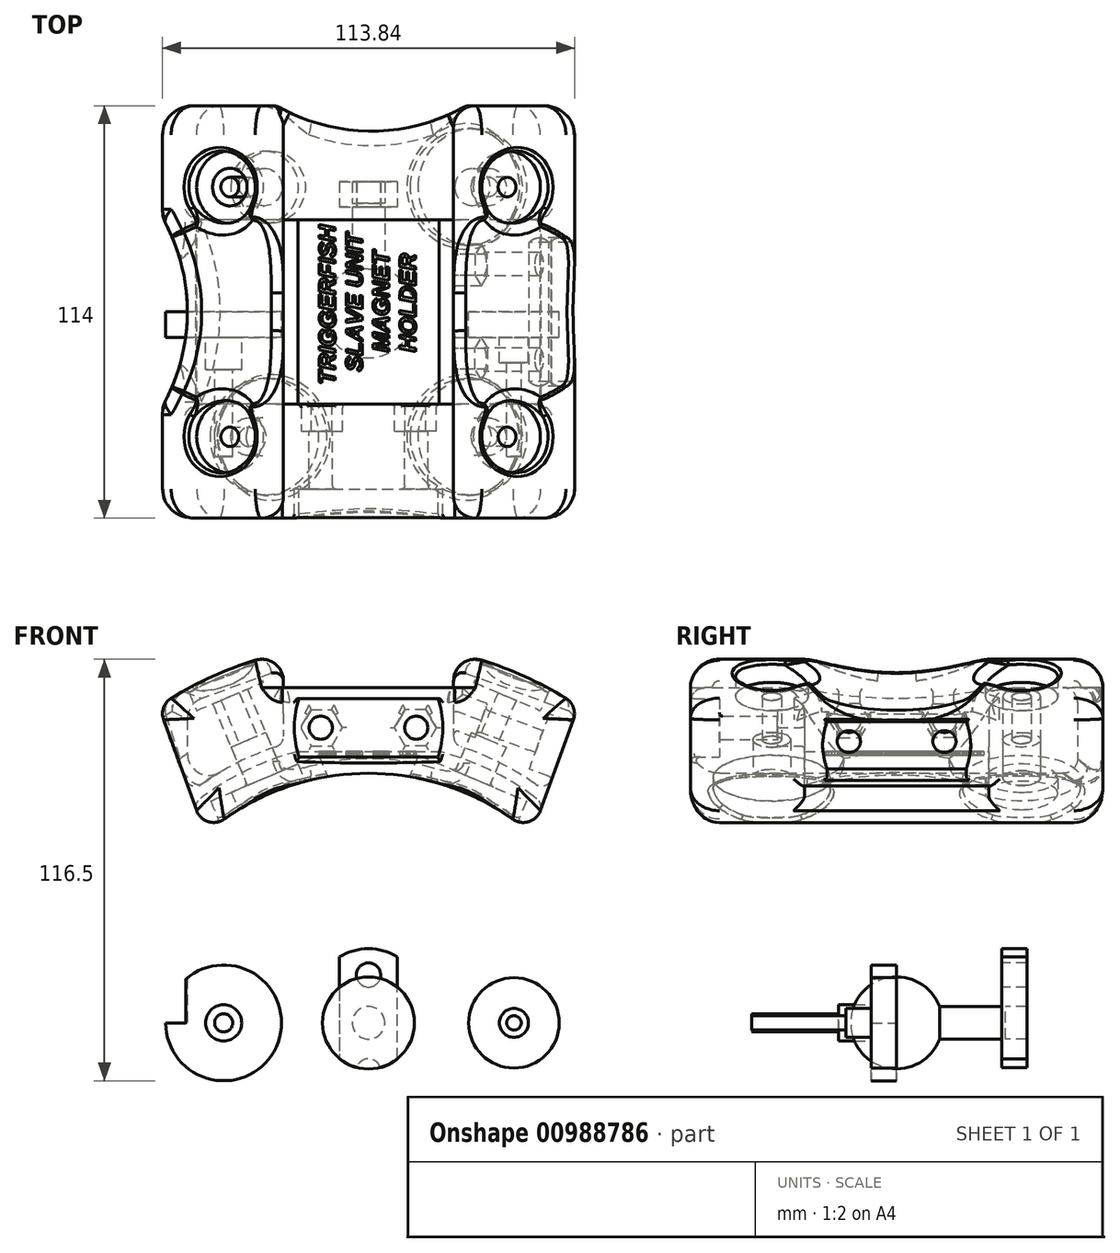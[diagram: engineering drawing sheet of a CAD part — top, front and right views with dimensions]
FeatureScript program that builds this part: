
annotation { "Feature Type Name" : "Feature", "Feature Type Description" : "" }
export const myFeature = defineFeature(function(context is Context, id is Id, definition is map)
    precondition{}
    {
        {
            var Q0;
            Q0=qCreatedBy(makeId("Front.planeOp"),FACE);
            var sketch = newSketch(context, id + "F0", { "sketchPlane" : qUnion([Q0])});
            skLineSegment(sketch, "E0", {"start": v(0, 0) * mm, "end": v(0, 44.71) * mm});
            skLineSegment(sketch, "E1", {"start": v(0, 44.71) * mm, "end": v(-36.6, 82.6) * mm});
            skLineSegment(sketch, "E2", {"start": v(0, 0) * mm, "end": v(-55, 0) * mm, "construction": true});
            skLineSegment(sketch, "E3.MirrorCS", {"start": v(0, 0) * mm, "end": v(55, 0) * mm, "construction": true});
            skArc(sketch, "E4", {"start": v(39.9, 56.3) * mm, "mid": v(0, 69) * mm, "end": v(-39.9, 56.3) * mm});
            skLineSegment(sketch, "E5", {"start": v(55.27, 80.07) * mm, "end": v(47.5, 58.66) * mm});
            skLineSegment(sketch, "E6.trimOffspring", {"start": v(-55, 41.67) * mm, "end": v(-55, 0) * mm, "construction": true});
            skArc(sketch, "E7", {"start": v(56.23, 82.7) * mm, "mid": v(0, 100) * mm, "end": v(-56.23, 82.7) * mm});
            skArc(sketch, "E8", {"start": v(54.51, 89.74) * mm, "mid": v(0, 105) * mm, "end": v(-54.51, 89.74) * mm});
            skLineSegment(sketch, "E9", {"start": v(55.27, 80.07) * mm, "end": v(56.61, 83.76) * mm});
            skLineSegment(sketch, "E10.MirrorCS", {"start": v(-55.27, 80.07) * mm, "end": v(-56.61, 83.76) * mm});
            skPoint(sketch, "E11.visualSharp", {"position": v(57.99, 87.54) * mm});
            skArc(sketch, "E11.filletArc", {"start": v(56.61, 83.76) * mm, "mid": v(56.63, 87.13) * mm, "end": v(54.51, 89.74) * mm});
            skPoint(sketch, "E12.visualSharp", {"position": v(-57.99, 87.54) * mm});
            skArc(sketch, "E12.filletArc", {"start": v(-54.51, 89.74) * mm, "mid": v(-56.63, 87.13) * mm, "end": v(-56.61, 83.76) * mm});
            skLineSegment(sketch, "E13", {"start": v(-55.27, 80.07) * mm, "end": v(-47.5, 58.66) * mm});
            skPoint(sketch, "E14.visualSharp", {"position": v(45.14, 52.19) * mm});
            skArc(sketch, "E14.filletArc", {"start": v(39.9, 56.3) * mm, "mid": v(44.28, 55.6) * mm, "end": v(47.5, 58.66) * mm});
            skPoint(sketch, "E15.visualSharp", {"position": v(-45.14, 52.19) * mm});
            skArc(sketch, "E15.filletArc", {"start": v(-47.5, 58.66) * mm, "mid": v(-44.28, 55.6) * mm, "end": v(-39.9, 56.3) * mm});
            skLineSegment(sketch, "E16.1.0.0", {"start": v(7.78, 66.12) * mm, "end": v(0, 44.71) * mm});
            skSolve(sketch);
        }
        {
            var Q0;
            {var subQ0=sQuery(id+"F0.wireOp",EDGE,"E5");Q0=makeQuery(id+"F0.imprint","IMPRINT",FACE,{"disambiguationData":[TD([[makeQuery(id+"F0.imprint","IMPRINT",EDGE,{"derivedFrom":subQ0}),-1.0]])]});}
            var Q1;
            Q1=makeQuery(id+"F0.imprint","IMPRINT",FACE,{"disambiguationData":[TD([[makeQuery(id+"F0.imprint","IMPRINT",EDGE,{"derivedFrom":sQuery(id+"F0.wireOp",EDGE,"E7")}),-1.0]])]});
            extrude(context, id + "F1", {"entities" : qUnion([Q0, Q1]), "endBound" : BoundingType.SYMMETRIC, "depth" : 114 * mm, "offsetDistance" : 25 * mm, "hasSecondDirection" : true, "secondDirectionOppositeDirection" : true, "secondDirectionDepth" : 53 * mm});
        }
        {
            var Q0;
            Q0=qCreatedBy(makeId("Right.planeOp"),FACE);
            var sketch = newSketch(context, id + "F2", { "sketchPlane" : qUnion([Q0])});
            skLineSegment(sketch, "E17", {"start": v(0, 0) * mm, "end": v(0, 150.3) * mm});
            skLineSegment(sketch, "E18", {"start": v(0, 0) * mm, "end": v(-50, 0) * mm});
            skLineSegment(sketch, "E19", {"start": v(0, 0) * mm, "end": v(50, 0) * mm});
            skLineSegment(sketch, "E20", {"start": v(50, 0) * mm, "end": v(35, 0) * mm});
            skLineSegment(sketch, "E21", {"start": v(-50, 0) * mm, "end": v(-35, 0) * mm});
            skLineSegment(sketch, "E22", {"start": v(-35, 0) * mm, "end": v(-35, 101.57) * mm});
            skLineSegment(sketch, "E23", {"start": v(35, 0) * mm, "end": v(35, 103.74) * mm});
            skLineSegment(sketch, "E24", {"start": v(35, 103.74) * mm, "end": v(-35, 103.74) * mm});
            skLineSegment(sketch, "E25", {"start": v(-35, 103.74) * mm, "end": v(-35, 101.57) * mm});
            skSolve(sketch);
        }
        {
            var Q0;
            Q0=sQuery(id+"F2.wireOp",EDGE,"E18");
            cPlane(context, id + "F3", {"entities" : qUnion([Q0]), "cplaneType" : CPlaneType.LINE_ANGLE, "offset" : 25 * mm, "angle" : 23 * degree, "width" : 150 * mm, "height" : 150 * mm});
        }
        {
            var Q0;
            Q0=qCreatedBy(id+"F3.planeOp",FACE);
            var sketch = newSketch(context, id + "F4", { "sketchPlane" : qUnion([Q0])});
            skLineSegment(sketch, "E26", {"start": v(0, -0.95) * mm, "end": v(0, 31.5) * mm});
            skCircle(sketch, "E27", {"center": v(0, 34.5) * mm, "radius": 2.7 * mm});
            skCircle(sketch, "E28", {"center": v(0, 34.5) * mm, "radius": 16.2 * mm});
            skCircle(sketch, "E29.MirrorC", {"center": v(0, -34.5) * mm, "radius": 2.7 * mm});
            skCircle(sketch, "E30.MirrorC", {"center": v(0, -34.5) * mm, "radius": 16.2 * mm});
            skCircle(sketch, "E31", {"center": v(0, 34.5) * mm, "radius": 5.2 * mm});
            skCircle(sketch, "E32", {"center": v(0, 34.5) * mm, "radius": 10 * mm});
            skCircle(sketch, "E33", {"center": v(0, -34.5) * mm, "radius": 10 * mm});
            skCircle(sketch, "E34", {"center": v(0, -34.5) * mm, "radius": 5.2 * mm});
            skSolve(sketch);
        }
        {
            var Q0;
            Q0=makeQuery(id+"F4.imprint","IMPRINT",FACE,{"disambiguationData":[TD([[makeQuery(id+"F4.imprint","IMPRINT",EDGE,{"derivedFrom":sQuery(id+"F4.wireOp",EDGE,"E27")}),1.0]])]});
            var Q1;
            Q1=makeQuery(id+"F4.imprint","IMPRINT",FACE,{"disambiguationData":[TD([[makeQuery(id+"F4.imprint","IMPRINT",EDGE,{"derivedFrom":sQuery(id+"F4.wireOp",EDGE,"E29.MirrorC")}),-1.0]])]});
            extrude(context, id + "F5", {"entities" : qUnion([Q0, Q1]), "operationType" : NewBodyOperationType.REMOVE, "endBound" : BoundingType.THROUGH_ALL, "oppositeDirection" : true, "depth" : 131 * mm, "offsetDistance" : 25 * mm});
        }
        {
            var Q0;
            Q0=makeQuery(id+"F4.imprint","IMPRINT",FACE,{"disambiguationData":[TD([[makeQuery(id+"F4.imprint","IMPRINT",EDGE,{"derivedFrom":sQuery(id+"F4.wireOp",EDGE,"7e92ca80-ed04-4259-94b1-b0eb367302a11.MirrorC")}),1.0]])]});
            var Q1;
            Q1=makeQuery(id+"F4.imprint","IMPRINT",FACE,{"disambiguationData":[TD([[makeQuery(id+"F4.imprint","IMPRINT",EDGE,{"derivedFrom":sQuery(id+"F4.wireOp",EDGE,"7e92ca80-ed04-4259-94b1-b0eb367302a11.MirrorC")}),-1.0]])]});
            var Q2;
            Q2=makeQuery(id+"F4.imprint","IMPRINT",FACE,{"disambiguationData":[TD([[makeQuery(id+"F4.imprint","IMPRINT",EDGE,{"derivedFrom":sQuery(id+"F4.wireOp",EDGE,"drXH0XQP-8KRI-Yurm-uRQJ-bzc3cydU0AWB")}),1.0]])]});
            var Q3;
            Q3=makeQuery(id+"F4.imprint","IMPRINT",FACE,{"disambiguationData":[TD([[makeQuery(id+"F4.imprint","IMPRINT",EDGE,{"derivedFrom":sQuery(id+"F4.wireOp",EDGE,"E27")}),-1.0]])]});
            var Q4;
            Q4=makeQuery(id+"F4.imprint","IMPRINT",FACE,{"disambiguationData":[TD([[makeQuery(id+"F4.imprint","IMPRINT",EDGE,{"derivedFrom":sQuery(id+"F4.wireOp",EDGE,"E30.MirrorC")}),-1.0]])]});
            var Q5;
            Q5=makeQuery(id+"F4.imprint","IMPRINT",FACE,{"disambiguationData":[TD([[makeQuery(id+"F4.imprint","IMPRINT",EDGE,{"derivedFrom":sQuery(id+"F4.wireOp",EDGE,"E28")}),1.0]])]});
            var Q6;
            Q6=makeQuery(id+"F4.imprint","IMPRINT",FACE,{"disambiguationData":[TD([[makeQuery(id+"F4.imprint","IMPRINT",EDGE,{"derivedFrom":sQuery(id+"F4.wireOp",EDGE,"E31")}),-1.0]])]});
            var Q7;
            Q7=makeQuery(id+"F4.imprint","IMPRINT",FACE,{"disambiguationData":[TD([[makeQuery(id+"F4.imprint","IMPRINT",EDGE,{"derivedFrom":sQuery(id+"F4.wireOp",EDGE,"iOXqjNKU-hcXU-oM97-z01q-G4LAReMeK2zs")}),-1.0]])]});
            var Q8;
            Q8=makeQuery(id+"F4.imprint","IMPRINT",FACE,{"disambiguationData":[TD([[makeQuery(id+"F4.imprint","IMPRINT",EDGE,{"derivedFrom":sQuery(id+"F4.wireOp",EDGE,"E33")}),1.0]])]});
            var Q9;
            Q9=makeQuery(id+"F4.imprint","IMPRINT",FACE,{"disambiguationData":[TD([[makeQuery(id+"F4.imprint","IMPRINT",EDGE,{"derivedFrom":sQuery(id+"F4.wireOp",EDGE,"E29.MirrorC")}),1.0]])]});
            extrude(context, id + "F6", {"entities" : qUnion([Q0, Q1, Q2, Q3, Q4, Q5, Q6, Q7, Q8, Q9]), "operationType" : NewBodyOperationType.REMOVE, "oppositeDirection" : true, "depth" : 73.5 * mm, "offsetDistance" : 25 * mm});
        }
        {
            var Q0;
            Q0=makeQuery(id+"F4.imprint","IMPRINT",FACE,{"disambiguationData":[TD([[makeQuery(id+"F4.imprint","IMPRINT",EDGE,{"derivedFrom":sQuery(id+"F4.wireOp",EDGE,"E27")}),-1.0]])]});
            var Q1;
            Q1=makeQuery(id+"F4.imprint","IMPRINT",FACE,{"disambiguationData":[TD([[makeQuery(id+"F4.imprint","IMPRINT",EDGE,{"derivedFrom":sQuery(id+"F4.wireOp",EDGE,"E29.MirrorC")}),1.0]])]});
            extrude(context, id + "F7", {"entities" : qUnion([Q0, Q1]), "operationType" : NewBodyOperationType.REMOVE, "oppositeDirection" : true, "depth" : 85 * mm, "hasOffset" : true, "offsetDistance" : 18 * mm});
        }
        {
            var Q0;
            Q0=makeQuery(id+"F4.imprint","IMPRINT",FACE,{"disambiguationData":[TD([[makeQuery(id+"F4.imprint","IMPRINT",EDGE,{"derivedFrom":sQuery(id+"F4.wireOp",EDGE,"7e92ca80-ed04-4259-94b1-b0eb367302a11.MirrorC")}),-1.0]])]});
            var Q1;
            Q1=makeQuery(id+"F4.imprint","IMPRINT",FACE,{"disambiguationData":[TD([[makeQuery(id+"F4.imprint","IMPRINT",EDGE,{"derivedFrom":sQuery(id+"F4.wireOp",EDGE,"E29.MirrorC")}),1.0]])]});
            var Q2;
            Q2=makeQuery(id+"F4.imprint","IMPRINT",FACE,{"disambiguationData":[TD([[makeQuery(id+"F4.imprint","IMPRINT",EDGE,{"derivedFrom":sQuery(id+"F4.wireOp",EDGE,"drXH0XQP-8KRI-Yurm-uRQJ-bzc3cydU0AWB")}),1.0]])]});
            var Q3;
            Q3=makeQuery(id+"F4.imprint","IMPRINT",FACE,{"disambiguationData":[TD([[makeQuery(id+"F4.imprint","IMPRINT",EDGE,{"derivedFrom":sQuery(id+"F4.wireOp",EDGE,"E27")}),-1.0]])]});
            var Q4;
            Q4=makeQuery(id+"F4.imprint","IMPRINT",FACE,{"disambiguationData":[TD([[makeQuery(id+"F4.imprint","IMPRINT",EDGE,{"derivedFrom":sQuery(id+"F4.wireOp",EDGE,"iOXqjNKU-hcXU-oM97-z01q-G4LAReMeK2zs")}),-1.0]])]});
            var Q5;
            Q5=makeQuery(id+"F4.imprint","IMPRINT",FACE,{"disambiguationData":[TD([[makeQuery(id+"F4.imprint","IMPRINT",EDGE,{"derivedFrom":sQuery(id+"F4.wireOp",EDGE,"E31")}),-1.0]])]});
            var Q6;
            Q6=makeQuery(id+"F4.imprint","IMPRINT",FACE,{"disambiguationData":[TD([[makeQuery(id+"F4.imprint","IMPRINT",EDGE,{"derivedFrom":sQuery(id+"F4.wireOp",EDGE,"E33")}),1.0]])]});
            extrude(context, id + "F8", {"entities" : qUnion([Q0, Q1, Q2, Q3, Q4, Q5, Q6]), "operationType" : NewBodyOperationType.REMOVE, "endBound" : BoundingType.THROUGH_ALL, "oppositeDirection" : true, "depth" : 25 * mm, "offsetDistance" : 25 * mm, "hasSecondDirection" : true, "secondDirectionOppositeDirection" : true, "secondDirectionDepth" : 98 * mm});
        }
        {
            var Q0;
            Q0=sQuery(id+"F4.wireOp",EDGE,"E26");
            cPlane(context, id + "F9", {"entities" : qUnion([Q0]), "cplaneType" : CPlaneType.LINE_ANGLE, "offset" : 25 * mm, "angle" : 23 * degree, "oppositeDirection" : true, "width" : 150 * mm, "height" : 150 * mm});
        }
        {
            var Q0;
            Q0=sQuery(id+"F2.wireOp",EDGE,"E18");
            cPlane(context, id + "F10", {"entities" : qUnion([Q0]), "cplaneType" : CPlaneType.LINE_ANGLE, "offset" : 25 * mm, "angle" : 104 * degree, "oppositeDirection" : true, "width" : 150 * mm, "height" : 150 * mm});
        }
        {
            var Q0;
            Q0=qCreatedBy(id+"F9.planeOp",FACE);
            var sketch = newSketch(context, id + "F11", { "sketchPlane" : qUnion([Q0])});
            skCircle(sketch, "E35", {"center": v(0, -34.5) * mm, "radius": 16.2 * mm});
            skCircle(sketch, "E36", {"center": v(0, -34.5) * mm, "radius": 10 * mm});
            skCircle(sketch, "E37", {"center": v(0, -34.5) * mm, "radius": 2.7 * mm});
            skCircle(sketch, "E38", {"center": v(0, 34.5) * mm, "radius": 2.7 * mm});
            skCircle(sketch, "E39", {"center": v(0, 34.5) * mm, "radius": 10 * mm});
            skCircle(sketch, "E40", {"center": v(0, 34.5) * mm, "radius": 16.2 * mm});
            skCircle(sketch, "E41", {"center": v(0, -34.5) * mm, "radius": 5.2 * mm});
            skCircle(sketch, "E42", {"center": v(0, 34.5) * mm, "radius": 5.2 * mm});
            skSolve(sketch);
        }
        {
            var Q0;
            Q0=makeQuery(id+"F11.imprint","IMPRINT",FACE,{"disambiguationData":[TD([[makeQuery(id+"F11.imprint","IMPRINT",EDGE,{"derivedFrom":sQuery(id+"F11.wireOp",EDGE,"E38")}),1.0]])]});
            var Q1;
            Q1=makeQuery(id+"F11.imprint","IMPRINT",FACE,{"disambiguationData":[TD([[makeQuery(id+"F11.imprint","IMPRINT",EDGE,{"derivedFrom":sQuery(id+"F11.wireOp",EDGE,"E37")}),1.0]])]});
            var Q2;
            Q2=sQuery(id+"F11.wireOp",EDGE,"E38");
            extrude(context, id + "F12", {"entities" : qUnion([Q0, Q1]), "operationType" : NewBodyOperationType.REMOVE, "surfaceEntities" : qUnion([Q2]), "endBound" : BoundingType.THROUGH_ALL, "oppositeDirection" : true, "depth" : 25 * mm, "offsetDistance" : 25 * mm});
        }
        {
            var Q0;
            Q0=makeQuery(id+"F11.imprint","IMPRINT",FACE,{"disambiguationData":[TD([[makeQuery(id+"F11.imprint","IMPRINT",EDGE,{"derivedFrom":sQuery(id+"F11.wireOp",EDGE,"E35")}),-1.0]])]});
            var Q1;
            Q1=makeQuery(id+"F11.imprint","IMPRINT",FACE,{"disambiguationData":[TD([[makeQuery(id+"F11.imprint","IMPRINT",EDGE,{"derivedFrom":sQuery(id+"F11.wireOp",EDGE,"E35")}),1.0]])]});
            var Q2;
            Q2=makeQuery(id+"F11.imprint","IMPRINT",FACE,{"disambiguationData":[TD([[makeQuery(id+"F11.imprint","IMPRINT",EDGE,{"derivedFrom":sQuery(id+"F11.wireOp",EDGE,"E39")}),-1.0]])]});
            var Q3;
            Q3=makeQuery(id+"F11.imprint","IMPRINT",FACE,{"disambiguationData":[TD([[makeQuery(id+"F11.imprint","IMPRINT",EDGE,{"derivedFrom":sQuery(id+"F11.wireOp",EDGE,"E39")}),1.0]])]});
            var Q4;
            Q4=makeQuery(id+"F11.imprint","IMPRINT",FACE,{"disambiguationData":[TD([[makeQuery(id+"F11.imprint","IMPRINT",EDGE,{"derivedFrom":sQuery(id+"F11.wireOp",EDGE,"E37")}),-1.0]])]});
            var Q5;
            Q5=makeQuery(id+"F11.imprint","IMPRINT",FACE,{"disambiguationData":[TD([[makeQuery(id+"F11.imprint","IMPRINT",EDGE,{"derivedFrom":sQuery(id+"F11.wireOp",EDGE,"E38")}),-1.0]])]});
            var Q6;
            Q6=makeQuery(id+"F11.imprint","IMPRINT",FACE,{"disambiguationData":[TD([[makeQuery(id+"F11.imprint","IMPRINT",EDGE,{"derivedFrom":sQuery(id+"F11.wireOp",EDGE,"E36")}),1.0]])]});
            var Q7;
            Q7=makeQuery(id+"F1.opExtrude","SWEPT_FACE",FACE,{"disambiguationData":[OSD([sQuery(id+"F0.wireOp",EDGE,"qRGGQMld-MaHZ-AlMi-78vc-qT90qwAjfGs4")])]});
            extrude(context, id + "F13", {"entities" : qUnion([Q0, Q1, Q2, Q3, Q4, Q5, Q6]), "operationType" : NewBodyOperationType.REMOVE, "oppositeDirection" : true, "depth" : 73.5 * mm, "endBoundEntityFace" : qUnion([Q7]), "offsetDistance" : 25 * mm});
        }
        {
            var Q0;
            Q0=sQuery(id+"F0.wireOp",EDGE,"E16.1.0.0");
            cPlane(context, id + "F14", {"entities" : qUnion([Q0]), "cplaneType" : CPlaneType.LINE_ANGLE, "offset" : 25 * mm, "angle" : 180 * degree, "width" : 150 * mm, "height" : 150 * mm});
        }
        {
            var Q0;
            Q0=makeQuery(id+"F11.imprint","IMPRINT",FACE,{"disambiguationData":[TD([[makeQuery(id+"F11.imprint","IMPRINT",EDGE,{"derivedFrom":sQuery(id+"F11.wireOp",EDGE,"E36")}),1.0]])]});
            var Q1;
            Q1=makeQuery(id+"F11.imprint","IMPRINT",FACE,{"disambiguationData":[TD([[makeQuery(id+"F11.imprint","IMPRINT",EDGE,{"derivedFrom":sQuery(id+"F11.wireOp",EDGE,"E37")}),-1.0]])]});
            var Q2;
            Q2=makeQuery(id+"F11.imprint","IMPRINT",FACE,{"disambiguationData":[TD([[makeQuery(id+"F11.imprint","IMPRINT",EDGE,{"derivedFrom":sQuery(id+"F11.wireOp",EDGE,"E39")}),1.0]])]});
            var Q3;
            Q3=makeQuery(id+"F11.imprint","IMPRINT",FACE,{"disambiguationData":[TD([[makeQuery(id+"F11.imprint","IMPRINT",EDGE,{"derivedFrom":sQuery(id+"F11.wireOp",EDGE,"E38")}),-1.0]])]});
            extrude(context, id + "F15", {"entities" : qUnion([Q0, Q1, Q2, Q3]), "operationType" : NewBodyOperationType.REMOVE, "endBound" : BoundingType.THROUGH_ALL, "oppositeDirection" : true, "depth" : 25 * mm, "offsetDistance" : 25 * mm, "hasSecondDirection" : true, "secondDirectionOppositeDirection" : true, "secondDirectionDepth" : 98 * mm});
        }
        {
            var Q0;
            Q0=makeQuery(id+"F11.imprint","IMPRINT",FACE,{"disambiguationData":[TD([[makeQuery(id+"F11.imprint","IMPRINT",EDGE,{"derivedFrom":sQuery(id+"F11.wireOp",EDGE,"E37")}),-1.0]])]});
            var Q1;
            Q1=makeQuery(id+"F11.imprint","IMPRINT",FACE,{"disambiguationData":[TD([[makeQuery(id+"F11.imprint","IMPRINT",EDGE,{"derivedFrom":sQuery(id+"F11.wireOp",EDGE,"E38")}),-1.0]])]});
            extrude(context, id + "F16", {"entities" : qUnion([Q0, Q1]), "operationType" : NewBodyOperationType.REMOVE, "oppositeDirection" : true, "depth" : 85 * mm, "offsetDistance" : 25 * mm});
        }
        {
            var Q0;
            Q0=qCreatedBy(makeId("Top.planeOp"),FACE);
            var sketch = newSketch(context, id + "F17", { "sketchPlane" : qUnion([Q0])});
            skLineSegment(sketch, "E43", {"start": v(40, 0) * mm, "end": v(40, -72) * mm});
            skLineSegment(sketch, "E44", {"start": v(40, -72) * mm, "end": v(-40, -72) * mm});
            skLineSegment(sketch, "E45", {"start": v(-40, -72) * mm, "end": v(-40, 72) * mm});
            skLineSegment(sketch, "E46", {"start": v(-40, 72) * mm, "end": v(40, 72) * mm});
            skLineSegment(sketch, "E47", {"start": v(40, 72) * mm, "end": v(40, 0) * mm});
            skLineSegment(sketch, "E48", {"start": v(0, 0) * mm, "end": v(-84.9, 0) * mm, "construction": true});
            skLineSegment(sketch, "E49", {"start": v(-40, -72) * mm, "end": v(-40, -52) * mm});
            skLineSegment(sketch, "E50", {"start": v(-40, -52) * mm, "end": v(-20, -52) * mm, "construction": true});
            skLineSegment(sketch, "E51", {"start": v(-20, -52) * mm, "end": v(20, -52) * mm, "construction": true});
            skLineSegment(sketch, "E52", {"start": v(20, -52) * mm, "end": v(40, -52) * mm, "construction": true});
            skLineSegment(sketch, "E53", {"start": v(0, 0) * mm, "end": v(55.62, 0) * mm, "construction": true});
            skArc(sketch, "E54", {"start": v(-40, -52) * mm, "mid": v(-34.14, -66.14) * mm, "end": v(-20, -72) * mm});
            skLineSegment(sketch, "E55", {"start": v(-40, 0) * mm, "end": v(-30, 0) * mm});
            skLineSegment(sketch, "E56", {"start": v(-40, 72) * mm, "end": v(-40, 52) * mm});
            skArc(sketch, "E57", {"start": v(-20, 72) * mm, "mid": v(-34.14, 66.14) * mm, "end": v(-40, 52) * mm});
            skFitSpline(sketch, "E58", {"points": [v(-40, -52) * mm, v(-30, 0) * mm, v(-40, 52) * mm], "startDerivative": vector(30, 104) * mm, "endDerivative": vector(-30, 104) * mm});
            skLineSegment(sketch, "E59", {"start": v(0, -30.04) * mm, "end": v(0, 13.28) * mm, "construction": true});
            skFitSpline(sketch, "E60.MirrorCS", {"points": [v(40, -52) * mm, v(30, 0) * mm, v(40, 52) * mm], "startDerivative": vector(-30, 104) * mm, "endDerivative": vector(30, 104) * mm});
            skArc(sketch, "E61.MirrorCS", {"start": v(40, -52) * mm, "mid": v(34.14, -66.14) * mm, "end": v(20, -72) * mm});
            skArc(sketch, "E62.MirrorCS", {"start": v(20, 72) * mm, "mid": v(34.14, 66.14) * mm, "end": v(40, 52) * mm});
            skLineSegment(sketch, "E63", {"start": v(0, -30.04) * mm, "end": v(0, -72) * mm, "construction": true});
            skLineSegment(sketch, "E64", {"start": v(0, -72) * mm, "end": v(0, -68.5) * mm, "construction": true});
            skArc(sketch, "E65", {"start": v(20, -72) * mm, "mid": v(0, -69.08) * mm, "end": v(-20, -72) * mm});
            skArc(sketch, "E66.MirrorCS", {"start": v(20, 72) * mm, "mid": v(0, 69.08) * mm, "end": v(-20, 72) * mm});
            skSolve(sketch);
        }
        {
            var Q0;
            Q0=qCreatedBy(id+"F14.planeOp",FACE);
            var sketch = newSketch(context, id + "F18", { "sketchPlane" : qUnion([Q0])});
            skLineSegment(sketch, "E67", {"start": v(-19.2, 81.07) * mm, "end": v(0, 81.07) * mm});
            skLineSegment(sketch, "E68", {"start": v(-19.2, 97.27) * mm, "end": v(19.2, 97.27) * mm});
            skLineSegment(sketch, "E69", {"start": v(19.2, 81.07) * mm, "end": v(0, 81.07) * mm});
            skPoint(sketch, "E70.endSnap0", {"position": v(-18.2, 89.17) * mm});
            skLineSegment(sketch, "E71.0", {"start": v(10.1, 94.17) * mm, "end": v(15.87, 94.17) * mm});
            skLineSegment(sketch, "E71.1", {"start": v(15.87, 94.17) * mm, "end": v(18.75, 89.17) * mm});
            skLineSegment(sketch, "E71.2", {"start": v(18.75, 89.17) * mm, "end": v(15.87, 84.17) * mm});
            skLineSegment(sketch, "E71.3", {"start": v(15.87, 84.17) * mm, "end": v(10.1, 84.17) * mm});
            skLineSegment(sketch, "E71.4", {"start": v(10.1, 84.17) * mm, "end": v(7.2, 89.17) * mm});
            skLineSegment(sketch, "E71.5", {"start": v(7.2, 89.17) * mm, "end": v(10.1, 94.17) * mm});
            skPoint(sketch, "E71.0.midPoint", {"position": v(11.28, 94.17) * mm});
            skLineSegment(sketch, "E72.MirrorCS", {"start": v(-15.87, 84.17) * mm, "end": v(-10.1, 84.17) * mm});
            skLineSegment(sketch, "E73.MirrorCS", {"start": v(-18.75, 89.17) * mm, "end": v(-15.87, 84.17) * mm});
            skLineSegment(sketch, "E74.MirrorCS", {"start": v(-15.87, 94.17) * mm, "end": v(-18.75, 89.17) * mm});
            skLineSegment(sketch, "E75.MirrorCS", {"start": v(-10.1, 94.17) * mm, "end": v(-15.87, 94.17) * mm});
            skLineSegment(sketch, "E76.MirrorCS", {"start": v(-10.1, 84.17) * mm, "end": v(-7.2, 89.17) * mm});
            skLineSegment(sketch, "E77.MirrorCS", {"start": v(-7.2, 89.17) * mm, "end": v(-10.1, 94.17) * mm});
            skLineSegment(sketch, "E78", {"start": v(0, 81.17) * mm, "end": v(0, 101.62) * mm, "construction": true});
            skArc(sketch, "E79", {"start": v(-19.2, 97.27) * mm, "mid": v(-20.5, 89.17) * mm, "end": v(-19.2, 81.07) * mm});
            skArc(sketch, "E80.MirrorCS", {"start": v(19.2, 97.27) * mm, "mid": v(20.5, 89.17) * mm, "end": v(19.2, 81.07) * mm});
            skCircle(sketch, "E81", {"center": v(-13.2, 89.17) * mm, "radius": 3.2 * mm});
            skCircle(sketch, "E82", {"center": v(13.2, 89.17) * mm, "radius": 3.2 * mm});
            skSolve(sketch);
        }
        {
            var Q0;
            {var subQ4=sQuery(id+"F18.wireOp",EDGE,"E69");Q0=makeQuery(id+"F18.imprint","IMPRINT",FACE,{"disambiguationData":[TD([[makeQuery(id+"F18.imprint","IMPRINT",EDGE,{"derivedFrom":subQ4}),-1.0]])]});}
            var Q1;
            {var subQ0=sQuery(id+"F18.wireOp",EDGE,"E67");Q1=makeQuery(id+"F18.imprint","IMPRINT",FACE,{"disambiguationData":[TD([[makeQuery(id+"F18.imprint","IMPRINT",EDGE,{"derivedFrom":subQ0}),1.0]])]});}
            var Q2;
            Q2=makeQuery(id+"F18.imprint","IMPRINT",FACE,{"disambiguationData":[TD([[makeQuery(id+"F18.imprint","IMPRINT",EDGE,{"derivedFrom":sQuery(id+"F18.wireOp",EDGE,"f1425f39-42cd-430a-935a-0037c350caf40.MirrorC")}),1.0]])]});
            var Q3;
            Q3=makeQuery(id+"F18.imprint","IMPRINT",FACE,{"disambiguationData":[TD([[makeQuery(id+"F18.imprint","IMPRINT",EDGE,{"derivedFrom":sQuery(id+"F18.wireOp",EDGE,"f1425f39-42cd-430a-935a-0037c350caf40.MirrorC")}),-1.0]])]});
            var Q4;
            Q4=makeQuery(id+"F18.imprint","IMPRINT",FACE,{"disambiguationData":[TD([[makeQuery(id+"F18.imprint","IMPRINT",EDGE,{"derivedFrom":sQuery(id+"F18.wireOp",EDGE,"a20799b0-e35e-4c22-ab32-daaa3fd97331")}),1.0]])]});
            var Q5;
            Q5=makeQuery(id+"F18.imprint","IMPRINT",FACE,{"disambiguationData":[TD([[makeQuery(id+"F18.imprint","IMPRINT",EDGE,{"derivedFrom":sQuery(id+"F18.wireOp",EDGE,"a20799b0-e35e-4c22-ab32-daaa3fd97331")}),-1.0]])]});
            var Q6;
            Q6=makeQuery(id+"F18.imprint","IMPRINT",FACE,{"disambiguationData":[TD([[makeQuery(id+"F18.imprint","IMPRINT",EDGE,{"derivedFrom":sQuery(id+"F18.wireOp",EDGE,"E71.0")}),-1.0]])]});
            var Q7;
            Q7=makeQuery(id+"F18.imprint","IMPRINT",FACE,{"disambiguationData":[TD([[makeQuery(id+"F18.imprint","IMPRINT",EDGE,{"derivedFrom":sQuery(id+"F18.wireOp",EDGE,"E72.MirrorCS")}),1.0]])]});
            extrude(context, id + "F19", {"entities" : qUnion([Q0, Q1, Q2, Q3, Q4, Q5, Q6, Q7]), "operationType" : NewBodyOperationType.REMOVE, "depth" : 65 * mm, "offsetDistance" : 25 * mm, "hasSecondDirection" : true, "secondDirectionOppositeDirection" : false, "secondDirectionDepth" : 33 * mm});
        }
        {
            var Q0;
            Q0=makeQuery(id+"F18.imprint","IMPRINT",FACE,{"disambiguationData":[TD([[makeQuery(id+"F18.imprint","IMPRINT",EDGE,{"derivedFrom":sQuery(id+"F18.wireOp",EDGE,"E82")}),1.0]])]});
            var Q1;
            Q1=makeQuery(id+"F18.imprint","IMPRINT",FACE,{"disambiguationData":[TD([[makeQuery(id+"F18.imprint","IMPRINT",EDGE,{"derivedFrom":sQuery(id+"F18.wireOp",EDGE,"E81")}),1.0]])]});
            extrude(context, id + "F20", {"entities" : qUnion([Q0, Q1]), "operationType" : NewBodyOperationType.REMOVE, "depth" : 76.3 * mm, "offsetDistance" : 25 * mm, "hasSecondDirection" : true, "secondDirectionOppositeDirection" : false, "secondDirectionDepth" : 0 * mm});
        }
        {
            var Q0;
            Q0=makeQuery(id+"F18.imprint","IMPRINT",FACE,{"disambiguationData":[TD([[makeQuery(id+"F18.imprint","IMPRINT",EDGE,{"derivedFrom":sQuery(id+"F18.wireOp",EDGE,"E72.MirrorCS")}),1.0]])]});
            var Q1;
            Q1=makeQuery(id+"F18.imprint","IMPRINT",FACE,{"disambiguationData":[TD([[makeQuery(id+"F18.imprint","IMPRINT",EDGE,{"derivedFrom":sQuery(id+"F18.wireOp",EDGE,"E81")}),1.0]])]});
            var Q2;
            Q2=makeQuery(id+"F18.imprint","IMPRINT",FACE,{"disambiguationData":[TD([[makeQuery(id+"F18.imprint","IMPRINT",EDGE,{"derivedFrom":sQuery(id+"F18.wireOp",EDGE,"E71.0")}),-1.0]])]});
            var Q3;
            Q3=makeQuery(id+"F18.imprint","IMPRINT",FACE,{"disambiguationData":[TD([[makeQuery(id+"F18.imprint","IMPRINT",EDGE,{"derivedFrom":sQuery(id+"F18.wireOp",EDGE,"E82")}),1.0]])]});
            extrude(context, id + "F21", {"entities" : qUnion([Q0, Q1, Q2, Q3]), "operationType" : NewBodyOperationType.REMOVE, "depth" : 16 * mm, "offsetDistance" : 25 * mm, "hasSecondDirection" : true, "secondDirectionOppositeDirection" : true, "secondDirectionDepth" : 4 * mm});
        }
        {
            var Q0;
            Q0=qCreatedBy(makeId("Top.planeOp"),FACE);
            var sketch = newSketch(context, id + "F22", { "sketchPlane" : qUnion([Q0])});
            skLineSegment(sketch, "E83", {"start": v(0, 0) * mm, "end": v(-25.5, 0) * mm, "construction": true});
            skLineSegment(sketch, "E84", {"start": v(0, 3.18) * mm, "end": v(0, -16.82) * mm, "construction": true});
            skLineSegment(sketch, "E85", {"start": v(-25.5, -25.5) * mm, "end": v(0, -25.5) * mm});
            skLineSegment(sketch, "E86.MirrorCS", {"start": v(-25.5, 25.5) * mm, "end": v(0, 25.5) * mm});
            skLineSegment(sketch, "E87.MirrorCS", {"start": v(0, -3.18) * mm, "end": v(0, 16.82) * mm, "construction": true});
            skLineSegment(sketch, "E88.MirrorCS", {"start": v(25.5, -25.5) * mm, "end": v(0, -25.5) * mm});
            skLineSegment(sketch, "E89.MirrorCS", {"start": v(25.5, 25.5) * mm, "end": v(0, 25.5) * mm});
            skLineSegment(sketch, "E90", {"start": v(-25.5, 57.15) * mm, "end": v(25.5, 57.15) * mm});
            skLineSegment(sketch, "E91.MirrorCS", {"start": v(-25.5, -57.15) * mm, "end": v(25.5, -57.15) * mm});
            skLineSegment(sketch, "E92", {"start": v(25.5, -25.5) * mm, "end": v(23.5, -25.5) * mm});
            skLineSegment(sketch, "E93", {"start": v(23.5, -25.5) * mm, "end": v(23.5, 57.15) * mm});
            skLineSegment(sketch, "E94", {"start": v(23.5, -25.5) * mm, "end": v(23.5, -57.15) * mm});
            skLineSegment(sketch, "E95.MirrorCS", {"start": v(-23.5, -25.5) * mm, "end": v(-23.5, 57.15) * mm});
            skLineSegment(sketch, "E96.MirrorCS", {"start": v(-23.5, -25.5) * mm, "end": v(-23.5, -57.15) * mm});
            skSolve(sketch);
        }
        {
            var Q0;
            {var subQ3=sQuery(id+"F22.wireOp",EDGE,"E86.MirrorCS");var subQ9=sQuery(id+"F22.wireOp",EDGE,"E95.MirrorCS");var subQ10=makeQuery(id+"F22.imprint","INTERSECT",VERTEX,{"derivedFrom":[subQ3,subQ9]});Q0=makeQuery(id+"F22.imprint","IMPRINT",FACE,{"disambiguationData":[TD([[makeQuery(id+"F22.imprint","IMPRINT",EDGE,{"disambiguationData":[TD([[subQ10,-1.0]])],"derivedFrom":subQ3}),-1.0]])]});}
            var Q1;
            {var subQ0=sQuery(id+"F22.wireOp",EDGE,"E94");Q1=makeQuery(id+"F22.imprint","IMPRINT",FACE,{"disambiguationData":[TD([[makeQuery(id+"F22.imprint","IMPRINT",EDGE,{"derivedFrom":subQ0}),-1.0]])]});}
            var Q2;
            {var subQ5=sQuery(id+"F22.wireOp",EDGE,"E95.MirrorCS");var subQ7=sQuery(id+"F22.wireOp",EDGE,"E86.MirrorCS");var subQ9=makeQuery(id+"F22.imprint","INTERSECT",VERTEX,{"derivedFrom":[subQ7,subQ5]});Q2=makeQuery(id+"F22.imprint","IMPRINT",FACE,{"disambiguationData":[TD([[makeQuery(id+"F22.imprint","IMPRINT",EDGE,{"disambiguationData":[TD([[subQ9,-1.0]])],"derivedFrom":subQ7}),1.0]])]});}
            extrude(context, id + "F23", {"entities" : qUnion([Q0, Q1, Q2]), "operationType" : NewBodyOperationType.REMOVE, "depth" : 110 * mm, "offsetDistance" : 25 * mm, "hasSecondDirection" : true, "secondDirectionOppositeDirection" : false, "secondDirectionDepth" : 92.6 * mm});
        }
        {
            var Q0;
            Q0=qCreatedBy(makeId("Top.planeOp"),FACE);
            var sketch = newSketch(context, id + "F24", { "sketchPlane" : qUnion([Q0])});
            skText(sketch, "E97", { "text": "   TRIGGERFISH \n     SLAVE UNIT\n        MAGNET \n        HOLDER", "fontName": "Arimo-BoldItalic.ttf"});
            const initialGuessF24  = {"E97": [-0.00916, -0.0254, 0, 1, 0.00464]};
            skSetInitialGuess(sketch, initialGuessF24);
            skSolve(sketch);
        }
        {
            var Q0;
            Q0=qSketchRegion(id+"F24",true);
            extrude(context, id + "F25", {"entities" : qUnion([Q0]), "operationType" : NewBodyOperationType.REMOVE, "depth" : 80 * mm, "hasOffset" : true, "offsetDistance" : 2 * mm, "hasSecondDirection" : true, "secondDirectionOppositeDirection" : false, "secondDirectionDepth" : 74 * mm});
        }
        {
            var Q0;
            Q0=sQuery(id+"F0.wireOp",EDGE,"E1");
            cPlane(context, id + "F26", {"entities" : qUnion([Q0]), "cplaneType" : CPlaneType.LINE_ANGLE, "offset" : 25 * mm, "angle" : 90 * degree, "width" : 150 * mm, "height" : 150 * mm});
        }
        {
            var Q0;
            Q0=qCreatedBy(makeId("Front.planeOp"),FACE);
            var sketch = newSketch(context, id + "F27", { "sketchPlane" : qUnion([Q0])});
            skCircle(sketch, "E98", {"center": v(40.19, 0) * mm, "radius": 12.5 * mm});
            skCircle(sketch, "E99", {"center": v(40.19, 0) * mm, "radius": 4 * mm});
            skCircle(sketch, "E100", {"center": v(40.19, 0) * mm, "radius": 2 * mm});
            skCircle(sketch, "E101", {"center": v(-40.03, 0) * mm, "radius": 16 * mm});
            skCircle(sketch, "E102", {"center": v(-40.03, 0) * mm, "radius": 5 * mm});
            skCircle(sketch, "E103", {"center": v(-40.03, 0) * mm, "radius": 2.5 * mm});
            skSolve(sketch);
        }
        {
            var Q0;
            Q0=qCreatedBy(makeId("Front.planeOp"),FACE);
            var sketch = newSketch(context, id + "F28", { "sketchPlane" : qUnion([Q0])});
            skLineSegment(sketch, "E104", {"start": v(-8, 20.5) * mm, "end": v(-8, -20.5) * mm});
            skLineSegment(sketch, "E105", {"start": v(8, -20.5) * mm, "end": v(8, 20.5) * mm});
            skLineSegment(sketch, "E106", {"start": v(0, 13.25) * mm, "end": v(0, 0) * mm, "construction": true});
            skLineSegment(sketch, "E107", {"start": v(0, 0) * mm, "end": v(0, -13.25) * mm, "construction": true});
            skCircle(sketch, "E108", {"center": v(0, 13.25) * mm, "radius": 3.35 * mm});
            skCircle(sketch, "E109", {"center": v(0, -13.25) * mm, "radius": 3.35 * mm});
            skLineSegment(sketch, "E110", {"start": v(-8, 0) * mm, "end": v(-8, 18.25) * mm, "construction": true});
            skLineSegment(sketch, "E111", {"start": v(-8, 0) * mm, "end": v(-8, -18.25) * mm, "construction": true});
            skLineSegment(sketch, "E112", {"start": v(-8, -18.25) * mm, "end": v(8, -18.25) * mm, "construction": true});
            skLineSegment(sketch, "E113", {"start": v(8, -18.25) * mm, "end": v(8, 18.25) * mm, "construction": true});
            skLineSegment(sketch, "E114", {"start": v(8, 18.25) * mm, "end": v(-8, 18.25) * mm, "construction": true});
            skArc(sketch, "E115", {"start": v(8, 18.25) * mm, "mid": v(0, 20.5) * mm, "end": v(-8, 18.25) * mm});
            skLineSegment(sketch, "E116", {"start": v(0, 0) * mm, "end": v(18.29, 0) * mm, "construction": true});
            skArc(sketch, "E117.MirrorCS", {"start": v(8, -18.25) * mm, "mid": v(0, -20.5) * mm, "end": v(-8, -18.25) * mm});
            skCircle(sketch, "E118", {"center": v(0, 0) * mm, "radius": 4.5 * mm});
            skCircle(sketch, "E119", {"center": v(0, 0) * mm, "radius": 12.8 * mm});
            skPoint(sketch, "E120", {"position": v(-12.8, 0) * mm});
            skSolve(sketch);
        }
        {
            var Q0;
            Q0=makeQuery(id+"F28.imprint","IMPRINT",FACE,{"disambiguationData":[TD([[makeQuery(id+"F28.imprint","IMPRINT",EDGE,{"derivedFrom":sQuery(id+"F28.wireOp",EDGE,"E118")}),1.0]])]});
            extrude(context, id + "F29", {"entities" : qUnion([Q0]), "oppositeDirection" : true, "depth" : 30 * mm, "offsetDistance" : 25 * mm, "hasSecondDirection" : true, "secondDirectionOppositeDirection" : true, "secondDirectionDepth" : 10 * mm});
        }
        {
            var Q0;
            Q0=makeQuery(id+"F27.imprint","IMPRINT",FACE,{"disambiguationData":[TD([[makeQuery(id+"F27.imprint","IMPRINT",EDGE,{"derivedFrom":sQuery(id+"F27.wireOp",EDGE,"E101")}),1.0]])]});
            var Q1;
            Q1=makeQuery(id+"F27.imprint","IMPRINT",FACE,{"disambiguationData":[TD([[makeQuery(id+"F27.imprint","IMPRINT",EDGE,{"derivedFrom":sQuery(id+"F27.wireOp",EDGE,"E102")}),1.0]])]});
            var Q2;
            Q2=makeQuery(id+"F27.imprint","IMPRINT",FACE,{"disambiguationData":[TD([[makeQuery(id+"F27.imprint","IMPRINT",EDGE,{"derivedFrom":sQuery(id+"F27.wireOp",EDGE,"E103")}),1.0]])]});
            extrude(context, id + "F30", {"entities" : qUnion([Q0, Q1, Q2]), "depth" : 7 * mm, "offsetDistance" : 25 * mm});
        }
        {
            var Q0;
            Q0=makeQuery(id+"F27.imprint","IMPRINT",FACE,{"disambiguationData":[TD([[makeQuery(id+"F27.imprint","IMPRINT",EDGE,{"derivedFrom":sQuery(id+"F27.wireOp",EDGE,"E102")}),1.0]])]});
            var Q1;
            Q1=makeQuery(id+"F27.imprint","IMPRINT",FACE,{"disambiguationData":[TD([[makeQuery(id+"F27.imprint","IMPRINT",EDGE,{"derivedFrom":sQuery(id+"F27.wireOp",EDGE,"E103")}),1.0]])]});
            extrude(context, id + "F31", {"entities" : qUnion([Q0, Q1]), "operationType" : NewBodyOperationType.ADD, "depth" : 16 * mm, "offsetDistance" : 25 * mm});
        }
        {
            var Q0;
            Q0=makeQuery(id+"F27.imprint","IMPRINT",FACE,{"disambiguationData":[TD([[makeQuery(id+"F27.imprint","IMPRINT",EDGE,{"derivedFrom":sQuery(id+"F27.wireOp",EDGE,"E103")}),1.0]])]});
            extrude(context, id + "F32", {"entities" : qUnion([Q0]), "operationType" : NewBodyOperationType.ADD, "depth" : 40 * mm, "offsetDistance" : 25 * mm});
        }
        {
            var Q0;
            Q0=makeQuery(id+"F27.imprint","IMPRINT",FACE,{"disambiguationData":[TD([[makeQuery(id+"F27.imprint","IMPRINT",EDGE,{"derivedFrom":sQuery(id+"F27.wireOp",EDGE,"E98")}),1.0]])]});
            var Q1;
            Q1=makeQuery(id+"F27.imprint","IMPRINT",FACE,{"disambiguationData":[TD([[makeQuery(id+"F27.imprint","IMPRINT",EDGE,{"derivedFrom":sQuery(id+"F27.wireOp",EDGE,"E99")}),1.0]])]});
            var Q2;
            Q2=makeQuery(id+"F27.imprint","IMPRINT",FACE,{"disambiguationData":[TD([[makeQuery(id+"F27.imprint","IMPRINT",EDGE,{"derivedFrom":sQuery(id+"F27.wireOp",EDGE,"E100")}),1.0]])]});
            extrude(context, id + "F33", {"entities" : qUnion([Q0, Q1, Q2]), "depth" : 7 * mm, "offsetDistance" : 25 * mm});
        }
        {
            var Q0;
            Q0=makeQuery(id+"F27.imprint","IMPRINT",FACE,{"disambiguationData":[TD([[makeQuery(id+"F27.imprint","IMPRINT",EDGE,{"derivedFrom":sQuery(id+"F27.wireOp",EDGE,"E99")}),1.0]])]});
            var Q1;
            Q1=makeQuery(id+"F27.imprint","IMPRINT",FACE,{"disambiguationData":[TD([[makeQuery(id+"F27.imprint","IMPRINT",EDGE,{"derivedFrom":sQuery(id+"F27.wireOp",EDGE,"E100")}),1.0]])]});
            extrude(context, id + "F34", {"entities" : qUnion([Q0, Q1]), "operationType" : NewBodyOperationType.ADD, "depth" : 14 * mm, "offsetDistance" : 25 * mm});
        }
        {
            var Q0;
            Q0=makeQuery(id+"F28.imprint","IMPRINT",FACE,{"disambiguationData":[TD([[makeQuery(id+"F28.imprint","IMPRINT",EDGE,{"derivedFrom":sQuery(id+"F28.wireOp",EDGE,"E108")}),-1.0]])]});
            var Q1;
            Q1=makeQuery(id+"F28.imprint","IMPRINT",FACE,{"disambiguationData":[TD([[makeQuery(id+"F28.imprint","IMPRINT",EDGE,{"derivedFrom":sQuery(id+"F28.wireOp",EDGE,"E118")}),-1.0]])]});
            var Q2;
            {var subQ0=sQuery(id+"F28.wireOp",EDGE,"E117.MirrorCS");Q2=makeQuery(id+"F28.imprint","IMPRINT",FACE,{"disambiguationData":[TD([[makeQuery(id+"F28.imprint","IMPRINT",EDGE,{"derivedFrom":subQ0}),-1.0]])]});}
            extrude(context, id + "F35", {"entities" : qUnion([Q0, Q1, Q2]), "operationType" : NewBodyOperationType.ADD, "oppositeDirection" : true, "depth" : 36 * mm, "offsetDistance" : 25 * mm, "hasSecondDirection" : true, "secondDirectionOppositeDirection" : true, "secondDirectionDepth" : 29 * mm});
        }
        {
            var Q0;
            Q0=qCreatedBy(makeId("Front.planeOp"),FACE);
            var sketch = newSketch(context, id + "F36", { "sketchPlane" : qUnion([Q0])});
            skLineSegment(sketch, "E121", {"start": v(0, 0) * mm, "end": v(59.5, 0) * mm, "construction": true});
            skLineSegment(sketch, "E122", {"start": v(12.7, 0) * mm, "end": v(-12.7, 0) * mm});
            skArc(sketch, "E123", {"start": v(12.7, 0) * mm, "mid": v(0, 12.7) * mm, "end": v(-12.7, 0) * mm});
            skSolve(sketch);
        }
        {
            var Q0;
            Q0=makeQuery(id+"F36.imprint","IMPRINT",FACE,{"disambiguationData":[TD([[makeQuery(id+"F36.imprint","IMPRINT",EDGE,{"derivedFrom":sQuery(id+"F36.wireOp",EDGE,"E122")}),-1.0]])]});
            var Q1;
            Q1=sQuery(id+"F36.wireOp",EDGE,"E121");
            revolve(context, id + "F37", {"operationType" : NewBodyOperationType.ADD, "surfaceOperationType" : NewSurfaceOperationType.NEW, "entities" : qUnion([Q0]), "axis" : qUnion([Q1]), "revolveType" : RevolveType.FULL});
        }
        {
            var Q0;
            Q0=makeQuery(id+"F27.imprint","IMPRINT",FACE,{"disambiguationData":[TD([[makeQuery(id+"F27.imprint","IMPRINT",EDGE,{"derivedFrom":sQuery(id+"F27.wireOp",EDGE,"E100")}),1.0]])]});
            extrude(context, id + "F38", {"entities" : qUnion([Q0]), "operationType" : NewBodyOperationType.ADD, "depth" : 40 * mm, "offsetDistance" : 25 * mm});
        }
        {
            var Q0;
            Q0=qCreatedBy(makeId("Front.planeOp"),FACE);
            var sketch = newSketch(context, id + "F39", { "sketchPlane" : qUnion([Q0])});
            skLineSegment(sketch, "E124", {"start": v(-19.2, 73.46) * mm, "end": v(0, 73.46) * mm});
            skLineSegment(sketch, "E125", {"start": v(-19.2, 89.66) * mm, "end": v(19.2, 89.66) * mm});
            skLineSegment(sketch, "E126", {"start": v(19.2, 73.46) * mm, "end": v(0, 73.46) * mm});
            skPoint(sketch, "E127.endSnap0", {"position": v(-18.2, 81.56) * mm});
            skLineSegment(sketch, "E128.0", {"start": v(10.1, 86.56) * mm, "end": v(15.87, 86.56) * mm});
            skLineSegment(sketch, "E128.1", {"start": v(15.87, 86.56) * mm, "end": v(18.75, 81.56) * mm});
            skLineSegment(sketch, "E128.2", {"start": v(18.75, 81.56) * mm, "end": v(15.87, 76.56) * mm});
            skLineSegment(sketch, "E128.3", {"start": v(15.87, 76.56) * mm, "end": v(10.1, 76.56) * mm});
            skLineSegment(sketch, "E128.4", {"start": v(10.1, 76.56) * mm, "end": v(7.2, 81.56) * mm});
            skLineSegment(sketch, "E128.5", {"start": v(7.2, 81.56) * mm, "end": v(10.1, 86.56) * mm});
            skPoint(sketch, "E128.0.midPoint", {"position": v(11.28, 86.56) * mm});
            skLineSegment(sketch, "E129.MirrorCS", {"start": v(-15.87, 76.56) * mm, "end": v(-10.1, 76.56) * mm});
            skLineSegment(sketch, "E130.MirrorCS", {"start": v(-18.75, 81.56) * mm, "end": v(-15.87, 76.56) * mm});
            skLineSegment(sketch, "E131.MirrorCS", {"start": v(-15.87, 86.56) * mm, "end": v(-18.75, 81.56) * mm});
            skLineSegment(sketch, "E132.MirrorCS", {"start": v(-10.1, 86.56) * mm, "end": v(-15.87, 86.56) * mm});
            skLineSegment(sketch, "E133.MirrorCS", {"start": v(-10.1, 76.56) * mm, "end": v(-7.2, 81.56) * mm});
            skLineSegment(sketch, "E134.MirrorCS", {"start": v(-7.2, 81.56) * mm, "end": v(-10.1, 86.56) * mm});
            skLineSegment(sketch, "E135", {"start": v(0, 73.56) * mm, "end": v(0, 94.01) * mm, "construction": true});
            skArc(sketch, "E136", {"start": v(-19.2, 89.66) * mm, "mid": v(-20.5, 81.56) * mm, "end": v(-19.2, 73.46) * mm});
            skArc(sketch, "E137.MirrorCS", {"start": v(19.2, 89.66) * mm, "mid": v(20.5, 81.56) * mm, "end": v(19.2, 73.46) * mm});
            skCircle(sketch, "E138", {"center": v(-13.2, 81.56) * mm, "radius": 3.2 * mm});
            skCircle(sketch, "E139", {"center": v(13.2, 81.56) * mm, "radius": 3.2 * mm});
            skSolve(sketch);
        }
        {
            var Q0;
            Q0=makeQuery(id+"F39.imprint","IMPRINT",FACE,{"disambiguationData":[TD([[makeQuery(id+"F39.imprint","IMPRINT",EDGE,{"derivedFrom":sQuery(id+"F39.wireOp",EDGE,"baad4e4c-4b0c-4cd4-9e59-b566b58eef68.MirrorC")}),1.0]])]});
            var Q1;
            Q1=makeQuery(id+"F39.imprint","IMPRINT",FACE,{"disambiguationData":[TD([[makeQuery(id+"F39.imprint","IMPRINT",EDGE,{"derivedFrom":sQuery(id+"F39.wireOp",EDGE,"baad4e4c-4b0c-4cd4-9e59-b566b58eef68.MirrorC")}),-1.0]])]});
            var Q2;
            Q2=makeQuery(id+"F39.imprint","IMPRINT",FACE,{"disambiguationData":[TD([[makeQuery(id+"F39.imprint","IMPRINT",EDGE,{"derivedFrom":sQuery(id+"F39.wireOp",EDGE,"E124")}),1.0]])]});
            var Q3;
            Q3=makeQuery(id+"F39.imprint","IMPRINT",FACE,{"disambiguationData":[TD([[makeQuery(id+"F39.imprint","IMPRINT",EDGE,{"derivedFrom":sQuery(id+"F39.wireOp",EDGE,"307c92be-7043-4664-b76b-6f5a6151604a")}),1.0]])]});
            var Q4;
            Q4=makeQuery(id+"F39.imprint","IMPRINT",FACE,{"disambiguationData":[TD([[makeQuery(id+"F39.imprint","IMPRINT",EDGE,{"derivedFrom":sQuery(id+"F39.wireOp",EDGE,"307c92be-7043-4664-b76b-6f5a6151604a")}),-1.0]])]});
            var Q5;
            Q5=makeQuery(id+"F39.imprint","IMPRINT",FACE,{"disambiguationData":[TD([[makeQuery(id+"F39.imprint","IMPRINT",EDGE,{"derivedFrom":sQuery(id+"F39.wireOp",EDGE,"E129.MirrorCS")}),1.0]])]});
            var Q6;
            Q6=makeQuery(id+"F39.imprint","IMPRINT",FACE,{"disambiguationData":[TD([[makeQuery(id+"F39.imprint","IMPRINT",EDGE,{"derivedFrom":sQuery(id+"F39.wireOp",EDGE,"E138")}),1.0]])]});
            var Q7;
            Q7=makeQuery(id+"F39.imprint","IMPRINT",FACE,{"disambiguationData":[TD([[makeQuery(id+"F39.imprint","IMPRINT",EDGE,{"derivedFrom":sQuery(id+"F39.wireOp",EDGE,"E128.0")}),-1.0]])]});
            var Q8;
            Q8=makeQuery(id+"F39.imprint","IMPRINT",FACE,{"disambiguationData":[TD([[makeQuery(id+"F39.imprint","IMPRINT",EDGE,{"derivedFrom":sQuery(id+"F39.wireOp",EDGE,"E139")}),1.0]])]});
            extrude(context, id + "F40", {"entities" : qUnion([Q0, Q1, Q2, Q3, Q4, Q5, Q6, Q7, Q8]), "operationType" : NewBodyOperationType.REMOVE, "depth" : 60 * mm, "offsetDistance" : 25 * mm, "hasSecondDirection" : true, "secondDirectionOppositeDirection" : false, "secondDirectionDepth" : 49 * mm});
        }
        {
            var Q0;
            Q0=makeQuery(id+"F39.imprint","IMPRINT",FACE,{"disambiguationData":[TD([[makeQuery(id+"F39.imprint","IMPRINT",EDGE,{"derivedFrom":sQuery(id+"F39.wireOp",EDGE,"E128.0")}),-1.0]])]});
            var Q1;
            Q1=makeQuery(id+"F39.imprint","IMPRINT",FACE,{"disambiguationData":[TD([[makeQuery(id+"F39.imprint","IMPRINT",EDGE,{"derivedFrom":sQuery(id+"F39.wireOp",EDGE,"E129.MirrorCS")}),1.0]])]});
            extrude(context, id + "F41", {"entities" : qUnion([Q0, Q1]), "operationType" : NewBodyOperationType.REMOVE, "depth" : 33 * mm, "offsetDistance" : 25 * mm, "hasSecondDirection" : true, "secondDirectionOppositeDirection" : false, "secondDirectionDepth" : 25 * mm});
        }
        {
            var Q0;
            Q0=makeQuery(id+"F39.imprint","IMPRINT",FACE,{"disambiguationData":[TD([[makeQuery(id+"F39.imprint","IMPRINT",EDGE,{"derivedFrom":sQuery(id+"F39.wireOp",EDGE,"E138")}),1.0]])]});
            var Q1;
            Q1=makeQuery(id+"F39.imprint","IMPRINT",FACE,{"disambiguationData":[TD([[makeQuery(id+"F39.imprint","IMPRINT",EDGE,{"derivedFrom":sQuery(id+"F39.wireOp",EDGE,"E139")}),1.0]])]});
            extrude(context, id + "F42", {"entities" : qUnion([Q0, Q1]), "operationType" : NewBodyOperationType.REMOVE, "depth" : 60 * mm, "offsetDistance" : 25 * mm, "hasSecondDirection" : true, "secondDirectionOppositeDirection" : false, "secondDirectionDepth" : 25 * mm});
        }
        {
            var Q0;
            Q0=qCreatedBy(makeId("Front.planeOp"),FACE);
            var sketch = newSketch(context, id + "F43", { "sketchPlane" : qUnion([Q0])});
            skLineSegment(sketch, "E140", {"start": v(0, 0) * mm, "end": v(-55, 0) * mm, "construction": true});
            skLineSegment(sketch, "E141", {"start": v(0, 98.96) * mm, "end": v(-55, 98.96) * mm, "construction": true});
            skLineSegment(sketch, "E142", {"start": v(-55, 98.96) * mm, "end": v(-55, 77.46) * mm, "construction": true});
            skLineSegment(sketch, "E143.MirrorCS", {"start": v(0, 98.96) * mm, "end": v(55, 98.96) * mm, "construction": true});
            skArc(sketch, "E144", {"start": v(50.08, 59.15) * mm, "mid": v(-0.13, 77.5) * mm, "end": v(-50.28, 58.98) * mm});
            skArc(sketch, "E145", {"start": v(51.3, 62.03) * mm, "mid": v(-0.49, 80.5) * mm, "end": v(-52.05, 61.4) * mm});
            skLineSegment(sketch, "E146", {"start": v(50.08, 59.15) * mm, "end": v(51.3, 62.03) * mm});
            skLineSegment(sketch, "E147", {"start": v(-50.28, 58.98) * mm, "end": v(-52.05, 61.4) * mm});
            skSolve(sketch);
        }
        {
            var Q0;
            {var subQ0=sQuery(id+"F43.wireOp",EDGE,"E144");Q0=makeQuery(id+"F43.imprint","IMPRINT",FACE,{"disambiguationData":[TD([[makeQuery(id+"F43.imprint","IMPRINT",EDGE,{"derivedFrom":subQ0}),-1.0]])]});}
            extrude(context, id + "F44", {"entities" : qUnion([Q0]), "operationType" : NewBodyOperationType.REMOVE, "endBound" : BoundingType.SYMMETRIC, "depth" : 51 * mm, "offsetDistance" : 25 * mm});
        }
        {
            var Q0;
            {var subQ0=sQuery(id+"F22.wireOp",EDGE,"E94");Q0=makeQuery(id+"F22.imprint","IMPRINT",FACE,{"disambiguationData":[TD([[makeQuery(id+"F22.imprint","IMPRINT",EDGE,{"derivedFrom":subQ0}),-1.0]])]});}
            var Q1;
            {var subQ5=sQuery(id+"F22.wireOp",EDGE,"E95.MirrorCS");var subQ7=sQuery(id+"F22.wireOp",EDGE,"E86.MirrorCS");var subQ9=makeQuery(id+"F22.imprint","INTERSECT",VERTEX,{"derivedFrom":[subQ7,subQ5]});Q1=makeQuery(id+"F22.imprint","IMPRINT",FACE,{"disambiguationData":[TD([[makeQuery(id+"F22.imprint","IMPRINT",EDGE,{"disambiguationData":[TD([[subQ9,-1.0]])],"derivedFrom":subQ7}),1.0]])]});}
            extrude(context, id + "F45", {"entities" : qUnion([Q0, Q1]), "operationType" : NewBodyOperationType.REMOVE, "depth" : 111 * mm, "offsetDistance" : 25 * mm, "hasSecondDirection" : true, "secondDirectionOppositeDirection" : false, "secondDirectionDepth" : 94 * mm});
        }
        {
            var Q0;
            Q0=makeQuery(id+"F1.opExtrude","CAP_EDGE",EDGE,{"disambiguationData":[OSD([sQuery(id+"F0.wireOp",EDGE,"E4")])],"isStart":false});
            var Q1;
            Q1=makeQuery(id+"F1.opExtrude","CAP_EDGE",EDGE,{"disambiguationData":[OSD([sQuery(id+"F0.wireOp",EDGE,"E4")])],"isStart":true});
            fillet(context, id + "F46", {"entities" : qUnion([Q0, Q1]), "radius" : 8 * mm, "tangentPropagation" : true, "allowEdgeOverflow" : false});
        }
        {
            var Q0;
            Q0=makeQuery(id+"F15.boolean.opBoolean","INTERSECT",EDGE,{"derivedFrom":[makeQuery(id+"F1.opExtrude","SWEPT_FACE",FACE,{"disambiguationData":[OSD([sQuery(id+"F0.wireOp",EDGE,"E8")])]}),makeQuery(id+"F15.opExtrude","SWEPT_FACE",FACE,{"disambiguationData":[OSD([sQuery(id+"F11.wireOp",EDGE,"E36")])]})]});
            var Q1;
            Q1=makeQuery(id+"F8.boolean.opBoolean","INTERSECT",EDGE,{"derivedFrom":[makeQuery(id+"F1.opExtrude","SWEPT_FACE",FACE,{"disambiguationData":[OSD([sQuery(id+"F0.wireOp",EDGE,"E8")])]}),makeQuery(id+"F8.opExtrude","SWEPT_FACE",FACE,{"disambiguationData":[OSD([sQuery(id+"F4.wireOp",EDGE,"E33")])]})]});
            var Q2;
            Q2=makeQuery(id+"F8.boolean.opBoolean","INTERSECT",EDGE,{"derivedFrom":[makeQuery(id+"F1.opExtrude","SWEPT_FACE",FACE,{"disambiguationData":[OSD([sQuery(id+"F0.wireOp",EDGE,"E8")])]}),makeQuery(id+"F8.opExtrude","SWEPT_FACE",FACE,{"disambiguationData":[OSD([sQuery(id+"F4.wireOp",EDGE,"E32")])]})]});
            var Q3;
            Q3=makeQuery(id+"F15.boolean.opBoolean","INTERSECT",EDGE,{"derivedFrom":[makeQuery(id+"F1.opExtrude","SWEPT_FACE",FACE,{"disambiguationData":[OSD([sQuery(id+"F0.wireOp",EDGE,"E8")])]}),makeQuery(id+"F15.opExtrude","SWEPT_FACE",FACE,{"disambiguationData":[OSD([sQuery(id+"F11.wireOp",EDGE,"E39")])]})]});
            var Q4;
            Q4=makeQuery(id+"F40.boolean.opBoolean","INTERSECT",EDGE,{"derivedFrom":[makeQuery(id+"F1.opExtrude","CAP_FACE",FACE,{"disambiguationData":[OSD([sQuery(id+"F0.wireOp",EDGE,"E4"),sQuery(id+"F0.wireOp",EDGE,"E5"),sQuery(id+"F0.wireOp",EDGE,"fb852597-ec99-4ae7-8949-f0fecbff0dff0.MirrorCS"),sQuery(id+"F0.wireOp",EDGE,"83a763b5-f6bf-4057-9b2f-e3cc2759ba8a.filletArc"),sQuery(id+"F0.wireOp",EDGE,"08ca167c-8c38-44c2-bc63-f0de48dad269.filletArc"),sQuery(id+"F0.wireOp",EDGE,"E8"),sQuery(id+"F0.wireOp",EDGE,"hLmCKB1O-Ida0-AmIF-oHOm-P1WSu6DwAWgH"),sQuery(id+"F0.wireOp",EDGE,"PErA75uU-YciE-L7wd-oDjI-uq8euoo5yPHw"),sQuery(id+"F0.wireOp",EDGE,"ed09322d-af04-475a-98f9-7beb472c6cf9.filletArc"),sQuery(id+"F0.wireOp",EDGE,"4c609844-175f-4688-9259-8d8842bf24b6.filletArc")])],"isStart":false}),makeQuery(id+"F40.opExtrude","SWEPT_FACE",FACE,{"disambiguationData":[OSD([sQuery(id+"F39.wireOp",EDGE,"E137.MirrorCS")])]})]});
            var Q5;
            Q5=makeQuery(id+"F42.boolean.opBoolean","INTERSECT",EDGE,{"derivedFrom":[makeQuery(id+"F40.boolean.opBoolean","COPY",FACE,{"derivedFrom":makeQuery(id+"F40.opExtrude","CAP_FACE",FACE,{"disambiguationData":[OSD([sQuery(id+"F39.wireOp",EDGE,"E124"),sQuery(id+"F39.wireOp",EDGE,"E125"),sQuery(id+"F39.wireOp",EDGE,"E126"),sQuery(id+"F39.wireOp",EDGE,"E136"),sQuery(id+"F39.wireOp",EDGE,"E137.MirrorCS")])],"isStart":true})}),makeQuery(id+"F42.opExtrude","SWEPT_FACE",FACE,{"disambiguationData":[OSD([sQuery(id+"F39.wireOp",EDGE,"E139")])]})]});
            var Q6;
            Q6=makeQuery(id+"F46.opFillet","BLEND_EDGE",EDGE,{"blendedFrom":[makeQuery(id+"F1.opExtrude","CAP_EDGE",EDGE,{"disambiguationData":[OSD([sQuery(id+"F0.wireOp",EDGE,"E4")])],"isStart":false}),makeQuery(id+"F40.boolean.opBoolean","COPY",FACE,{"derivedFrom":makeQuery(id+"F40.opExtrude","SWEPT_FACE",FACE,{"disambiguationData":[OSD([sQuery(id+"F39.wireOp",EDGE,"E124"),sQuery(id+"F39.wireOp",EDGE,"E126")])]})})],"blendedInto":[makeQuery(id+"F40.boolean.opBoolean","COPY",FACE,{"derivedFrom":makeQuery(id+"F40.opExtrude","SWEPT_FACE",FACE,{"disambiguationData":[OSD([sQuery(id+"F39.wireOp",EDGE,"E124"),sQuery(id+"F39.wireOp",EDGE,"E126")])]})})]});
            var Q7;
            Q7=makeQuery(id+"F40.boolean.opBoolean","INTERSECT",EDGE,{"derivedFrom":[makeQuery(id+"F1.opExtrude","CAP_FACE",FACE,{"disambiguationData":[OSD([sQuery(id+"F0.wireOp",EDGE,"E4"),sQuery(id+"F0.wireOp",EDGE,"E5"),sQuery(id+"F0.wireOp",EDGE,"fb852597-ec99-4ae7-8949-f0fecbff0dff0.MirrorCS"),sQuery(id+"F0.wireOp",EDGE,"83a763b5-f6bf-4057-9b2f-e3cc2759ba8a.filletArc"),sQuery(id+"F0.wireOp",EDGE,"08ca167c-8c38-44c2-bc63-f0de48dad269.filletArc"),sQuery(id+"F0.wireOp",EDGE,"E8"),sQuery(id+"F0.wireOp",EDGE,"hLmCKB1O-Ida0-AmIF-oHOm-P1WSu6DwAWgH"),sQuery(id+"F0.wireOp",EDGE,"PErA75uU-YciE-L7wd-oDjI-uq8euoo5yPHw"),sQuery(id+"F0.wireOp",EDGE,"ed09322d-af04-475a-98f9-7beb472c6cf9.filletArc"),sQuery(id+"F0.wireOp",EDGE,"4c609844-175f-4688-9259-8d8842bf24b6.filletArc")])],"isStart":false}),makeQuery(id+"F40.opExtrude","SWEPT_FACE",FACE,{"disambiguationData":[OSD([sQuery(id+"F39.wireOp",EDGE,"E136")])]})]});
            var Q8;
            Q8=makeQuery(id+"F42.boolean.opBoolean","INTERSECT",EDGE,{"derivedFrom":[makeQuery(id+"F40.boolean.opBoolean","COPY",FACE,{"derivedFrom":makeQuery(id+"F40.opExtrude","CAP_FACE",FACE,{"disambiguationData":[OSD([sQuery(id+"F39.wireOp",EDGE,"E124"),sQuery(id+"F39.wireOp",EDGE,"E125"),sQuery(id+"F39.wireOp",EDGE,"E126"),sQuery(id+"F39.wireOp",EDGE,"E136"),sQuery(id+"F39.wireOp",EDGE,"E137.MirrorCS")])],"isStart":true})}),makeQuery(id+"F42.opExtrude","SWEPT_FACE",FACE,{"disambiguationData":[OSD([sQuery(id+"F39.wireOp",EDGE,"E138")])]})]});
            var Q9;
            Q9=makeQuery(id+"F41.boolean.opBoolean","COPY",EDGE,{"derivedFrom":makeQuery(id+"F41.opExtrude","CAP_EDGE",EDGE,{"disambiguationData":[OSD([sQuery(id+"F39.wireOp",EDGE,"E139")])],"isStart":false})});
            var Q10;
            Q10=makeQuery(id+"F41.boolean.opBoolean","COPY",EDGE,{"derivedFrom":makeQuery(id+"F41.opExtrude","CAP_EDGE",EDGE,{"disambiguationData":[OSD([sQuery(id+"F39.wireOp",EDGE,"E138")])],"isStart":false})});
            var Q11;
            Q11=makeQuery(id+"F21.boolean.opBoolean","INTERSECT",EDGE,{"derivedFrom":[makeQuery(id+"F20.boolean.opBoolean","COPY",FACE,{"derivedFrom":makeQuery(id+"F20.opExtrude","SWEPT_FACE",FACE,{"disambiguationData":[OSD([sQuery(id+"F18.wireOp",EDGE,"E81")])]})}),makeQuery(id+"F21.opExtrude","CAP_FACE",FACE,{"disambiguationData":[OSD([sQuery(id+"F18.wireOp",EDGE,"E72.MirrorCS"),sQuery(id+"F18.wireOp",EDGE,"E73.MirrorCS"),sQuery(id+"F18.wireOp",EDGE,"E74.MirrorCS"),sQuery(id+"F18.wireOp",EDGE,"E75.MirrorCS"),sQuery(id+"F18.wireOp",EDGE,"E76.MirrorCS"),sQuery(id+"F18.wireOp",EDGE,"E77.MirrorCS")])],"isStart":false})]});
            var Q12;
            Q12=makeQuery(id+"F21.boolean.opBoolean","INTERSECT",EDGE,{"derivedFrom":[makeQuery(id+"F20.boolean.opBoolean","COPY",FACE,{"derivedFrom":makeQuery(id+"F20.opExtrude","SWEPT_FACE",FACE,{"disambiguationData":[OSD([sQuery(id+"F18.wireOp",EDGE,"E82")])]})}),makeQuery(id+"F21.opExtrude","CAP_FACE",FACE,{"disambiguationData":[OSD([sQuery(id+"F18.wireOp",EDGE,"E71.0"),sQuery(id+"F18.wireOp",EDGE,"E71.1"),sQuery(id+"F18.wireOp",EDGE,"E71.2"),sQuery(id+"F18.wireOp",EDGE,"E71.3"),sQuery(id+"F18.wireOp",EDGE,"E71.4"),sQuery(id+"F18.wireOp",EDGE,"E71.5")])],"isStart":false})]});
            var Q13;
            Q13=makeQuery(id+"F15.boolean.opBoolean","COPY",EDGE,{"derivedFrom":makeQuery(id+"F15.opExtrude","CAP_EDGE",EDGE,{"disambiguationData":[OSD([sQuery(id+"F11.wireOp",EDGE,"E38")])],"isStart":true})});
            var Q14;
            Q14=makeQuery(id+"F8.boolean.opBoolean","COPY",EDGE,{"derivedFrom":makeQuery(id+"F8.opExtrude","CAP_EDGE",EDGE,{"disambiguationData":[OSD([sQuery(id+"F4.wireOp",EDGE,"E27")])],"isStart":true})});
            var Q15;
            Q15=makeQuery(id+"F8.boolean.opBoolean","COPY",EDGE,{"derivedFrom":makeQuery(id+"F8.opExtrude","CAP_EDGE",EDGE,{"disambiguationData":[OSD([sQuery(id+"F4.wireOp",EDGE,"E29.MirrorC")])],"isStart":true})});
            var Q16;
            Q16=makeQuery(id+"F15.boolean.opBoolean","COPY",EDGE,{"derivedFrom":makeQuery(id+"F15.opExtrude","CAP_EDGE",EDGE,{"disambiguationData":[OSD([sQuery(id+"F11.wireOp",EDGE,"E37")])],"isStart":true})});
            var Q17;
            Q17=makeQuery(id+"F7.boolean.opBoolean","INTERSECT",EDGE,{"derivedFrom":[makeQuery(id+"F6.boolean.opBoolean","COPY",FACE,{"derivedFrom":makeQuery(id+"F6.opExtrude","CAP_FACE",FACE,{"disambiguationData":[OSD([sQuery(id+"F4.wireOp",EDGE,"E29.MirrorC"),sQuery(id+"F4.wireOp",EDGE,"E30.MirrorC")])],"isStart":false})}),makeQuery(id+"F7.opExtrude","SWEPT_FACE",FACE,{"disambiguationData":[OSD([sQuery(id+"F4.wireOp",EDGE,"E34")])]})]});
            var Q18;
            Q18=makeQuery(id+"F16.boolean.opBoolean","INTERSECT",EDGE,{"derivedFrom":[makeQuery(id+"F13.boolean.opBoolean","COPY",FACE,{"derivedFrom":makeQuery(id+"F13.opExtrude","CAP_FACE",FACE,{"disambiguationData":[OSD([sQuery(id+"F11.wireOp",EDGE,"E38"),sQuery(id+"F11.wireOp",EDGE,"E40")])],"isStart":false})}),makeQuery(id+"F16.opExtrude","SWEPT_FACE",FACE,{"disambiguationData":[OSD([sQuery(id+"F11.wireOp",EDGE,"E42")])]})]});
            var Q19;
            Q19=makeQuery(id+"F7.boolean.opBoolean","INTERSECT",EDGE,{"derivedFrom":[makeQuery(id+"F6.boolean.opBoolean","COPY",FACE,{"derivedFrom":makeQuery(id+"F6.opExtrude","CAP_FACE",FACE,{"disambiguationData":[OSD([sQuery(id+"F4.wireOp",EDGE,"E27"),sQuery(id+"F4.wireOp",EDGE,"E28")])],"isStart":false})}),makeQuery(id+"F7.opExtrude","SWEPT_FACE",FACE,{"disambiguationData":[OSD([sQuery(id+"F4.wireOp",EDGE,"E31")])]})]});
            var Q20;
            Q20=makeQuery(id+"F7.boolean.opBoolean","COPY",EDGE,{"derivedFrom":makeQuery(id+"F7.opExtrude","CAP_EDGE",EDGE,{"disambiguationData":[OSD([sQuery(id+"F4.wireOp",EDGE,"E29.MirrorC")])],"isStart":false})});
            fillet(context, id + "F47", {"entities" : qUnion([Q0, Q1, Q2, Q3, Q4, Q5, Q6, Q7, Q8, Q9, Q10, Q11, Q12, Q13, Q14, Q15, Q16, Q17, Q18, Q19, Q20]), "radius" : 1 * mm, "tangentPropagation" : true, "allowEdgeOverflow" : false});
        }
        {
            var Q0;
            {var subQ3=sQuery(id+"F22.wireOp",EDGE,"E86.MirrorCS");var subQ9=sQuery(id+"F22.wireOp",EDGE,"E95.MirrorCS");var subQ10=makeQuery(id+"F22.imprint","INTERSECT",VERTEX,{"derivedFrom":[subQ3,subQ9]});Q0=makeQuery(id+"F22.imprint","IMPRINT",FACE,{"disambiguationData":[TD([[makeQuery(id+"F22.imprint","IMPRINT",EDGE,{"disambiguationData":[TD([[subQ10,-1.0]])],"derivedFrom":subQ3}),-1.0]])]});}
            var Q1;
            Q1=makeQuery(id+"F21.boolean.opBoolean","COPY",FACE,{"derivedFrom":makeQuery(id+"F21.opExtrude","SWEPT_FACE",FACE,{"disambiguationData":[OSD([sQuery(id+"F18.wireOp",EDGE,"E72.MirrorCS")])]})});
            extrude(context, id + "F48", {"entities" : qUnion([Q0, Q1]), "operationType" : NewBodyOperationType.REMOVE, "depth" : 120.9 * mm, "offsetDistance" : 25 * mm, "hasSecondDirection" : true, "secondDirectionOppositeDirection" : false, "secondDirectionDepth" : 75 * mm});
        }
        {
            var Q0;
            Q0=makeQuery(id+"F45.boolean.opBoolean","INTERSECT",EDGE,{"derivedFrom":[makeQuery(id+"F45.opExtrude","SWEPT_FACE",FACE,{"disambiguationData":[OSD([sQuery(id+"F22.wireOp",EDGE,"E95.MirrorCS")])]}),makeQuery(id+"F45.opExtrude","SWEPT_FACE",FACE,{"disambiguationData":[OSD([sQuery(id+"F22.wireOp",EDGE,"E96.MirrorCS")])]})]});
            var Q1;
            Q1=makeQuery(id+"F45.boolean.opBoolean","INTERSECT",EDGE,{"derivedFrom":[makeQuery(id+"F45.opExtrude","SWEPT_FACE",FACE,{"disambiguationData":[OSD([sQuery(id+"F22.wireOp",EDGE,"E93")])]}),makeQuery(id+"F45.opExtrude","SWEPT_FACE",FACE,{"disambiguationData":[OSD([sQuery(id+"F22.wireOp",EDGE,"E94")])]})]});
            fillet(context, id + "F49", {"entities" : qUnion([Q0, Q1]), "radius" : 6 * mm, "tangentPropagation" : true, "allowEdgeOverflow" : false});
        }
        {
            var Q0;
            Q0=makeQuery(id+"F48.boolean.opBoolean","INTERSECT",EDGE,{"derivedFrom":[makeQuery(id+"F23.boolean.opBoolean","COPY",FACE,{"derivedFrom":makeQuery(id+"F23.opExtrude","CAP_FACE",FACE,{"disambiguationData":[OSD([sQuery(id+"F22.wireOp",EDGE,"E90"),sQuery(id+"F22.wireOp",EDGE,"E91.MirrorCS"),sQuery(id+"F22.wireOp",EDGE,"E93"),sQuery(id+"F22.wireOp",EDGE,"E94"),sQuery(id+"F22.wireOp",EDGE,"E95.MirrorCS"),sQuery(id+"F22.wireOp",EDGE,"E96.MirrorCS")])],"isStart":true})}),makeQuery(id+"F48.opExtrude","SWEPT_FACE",FACE,{"disambiguationData":[OSD([sQuery(id+"F22.wireOp",EDGE,"E86.MirrorCS"),sQuery(id+"F22.wireOp",EDGE,"E89.MirrorCS")])]})]});
            var Q1;
            Q1=makeQuery(id+"F48.boolean.opBoolean","INTERSECT",EDGE,{"derivedFrom":[makeQuery(id+"F23.boolean.opBoolean","COPY",FACE,{"derivedFrom":makeQuery(id+"F23.opExtrude","CAP_FACE",FACE,{"disambiguationData":[OSD([sQuery(id+"F22.wireOp",EDGE,"E90"),sQuery(id+"F22.wireOp",EDGE,"E91.MirrorCS"),sQuery(id+"F22.wireOp",EDGE,"E93"),sQuery(id+"F22.wireOp",EDGE,"E94"),sQuery(id+"F22.wireOp",EDGE,"E95.MirrorCS"),sQuery(id+"F22.wireOp",EDGE,"E96.MirrorCS")])],"isStart":true})}),makeQuery(id+"F48.opExtrude","SWEPT_FACE",FACE,{"disambiguationData":[OSD([sQuery(id+"F22.wireOp",EDGE,"E85"),sQuery(id+"F22.wireOp",EDGE,"E88.MirrorCS")])]})]});
            fillet(context, id + "F50", {"entities" : qUnion([Q0, Q1]), "radius" : 7 * mm, "tangentPropagation" : true, "allowEdgeOverflow" : false});
        }
        {
            var Q0;
            Q0=makeQuery(id+"F23.boolean.opBoolean","INTERSECT",EDGE,{"derivedFrom":[makeQuery(id+"F1.opExtrude","CAP_FACE",FACE,{"disambiguationData":[OSD([sQuery(id+"F0.wireOp",EDGE,"E4"),sQuery(id+"F0.wireOp",EDGE,"E5"),sQuery(id+"F0.wireOp",EDGE,"E8"),sQuery(id+"F0.wireOp",EDGE,"E9"),sQuery(id+"F0.wireOp",EDGE,"E10.MirrorCS"),sQuery(id+"F0.wireOp",EDGE,"E11.filletArc"),sQuery(id+"F0.wireOp",EDGE,"E12.filletArc"),sQuery(id+"F0.wireOp",EDGE,"E13"),sQuery(id+"F0.wireOp",EDGE,"E14.filletArc"),sQuery(id+"F0.wireOp",EDGE,"E15.filletArc")])],"isStart":false}),makeQuery(id+"F23.opExtrude","CAP_FACE",FACE,{"disambiguationData":[OSD([sQuery(id+"F22.wireOp",EDGE,"E90"),sQuery(id+"F22.wireOp",EDGE,"E91.MirrorCS"),sQuery(id+"F22.wireOp",EDGE,"E93"),sQuery(id+"F22.wireOp",EDGE,"E94"),sQuery(id+"F22.wireOp",EDGE,"E95.MirrorCS"),sQuery(id+"F22.wireOp",EDGE,"E96.MirrorCS")])],"isStart":true})]});
            var Q1;
            Q1=makeQuery(id+"F23.boolean.opBoolean","INTERSECT",EDGE,{"derivedFrom":[makeQuery(id+"F1.opExtrude","CAP_FACE",FACE,{"disambiguationData":[OSD([sQuery(id+"F0.wireOp",EDGE,"E4"),sQuery(id+"F0.wireOp",EDGE,"E5"),sQuery(id+"F0.wireOp",EDGE,"E8"),sQuery(id+"F0.wireOp",EDGE,"E9"),sQuery(id+"F0.wireOp",EDGE,"E10.MirrorCS"),sQuery(id+"F0.wireOp",EDGE,"E11.filletArc"),sQuery(id+"F0.wireOp",EDGE,"E12.filletArc"),sQuery(id+"F0.wireOp",EDGE,"E13"),sQuery(id+"F0.wireOp",EDGE,"E14.filletArc"),sQuery(id+"F0.wireOp",EDGE,"E15.filletArc")])],"isStart":true}),makeQuery(id+"F23.opExtrude","CAP_FACE",FACE,{"disambiguationData":[OSD([sQuery(id+"F22.wireOp",EDGE,"E90"),sQuery(id+"F22.wireOp",EDGE,"E91.MirrorCS"),sQuery(id+"F22.wireOp",EDGE,"E93"),sQuery(id+"F22.wireOp",EDGE,"E94"),sQuery(id+"F22.wireOp",EDGE,"E95.MirrorCS"),sQuery(id+"F22.wireOp",EDGE,"E96.MirrorCS")])],"isStart":true})]});
            fillet(context, id + "F51", {"entities" : qUnion([Q0, Q1]), "radius" : 4 * mm, "tangentPropagation" : true, "allowEdgeOverflow" : false});
        }
        {
            var Q0;
            Q0=makeQuery(id+"F1.opExtrude","SWEPT_FACE",FACE,{"disambiguationData":[OSD([sQuery(id+"F0.wireOp",EDGE,"E10.MirrorCS"),sQuery(id+"F0.wireOp",EDGE,"E13")])]});
            var sketch = newSketch(context, id + "F52", { "sketchPlane" : qUnion([Q0])});
            skLineSegment(sketch, "E148", {"start": v(-24, 109.24) * mm, "end": v(24, 109.24) * mm});
            skArc(sketch, "E149", {"start": v(-24, 104.24) * mm, "mid": v(0, 100) * mm, "end": v(24, 104.24) * mm});
            skArc(sketch, "E150", {"start": v(-34.76, 109.24) * mm, "mid": v(0, 100) * mm, "end": v(34.76, 109.24) * mm});
            skLineSegment(sketch, "E151", {"start": v(-24, 109.24) * mm, "end": v(-34.76, 109.24) * mm});
            skLineSegment(sketch, "E152", {"start": v(24, 109.24) * mm, "end": v(34.76, 109.24) * mm});
            skLineSegment(sketch, "E153", {"start": v(-48, 98.06) * mm, "end": v(-48, 109.24) * mm});
            skLineSegment(sketch, "E154", {"start": v(-48, 109.24) * mm, "end": v(-34.76, 109.24) * mm});
            skLineSegment(sketch, "E155", {"start": v(-49, 71.36) * mm, "end": v(-49, 84.71) * mm});
            skLineSegment(sketch, "E156", {"start": v(-49, 84.71) * mm, "end": v(-49, 98.06) * mm});
            skSolve(sketch);
        }
        {
            var Q0;
            Q0=makeQuery(id+"F52.imprint","IMPRINT",FACE,{"disambiguationData":[TD([[makeQuery(id+"F52.imprint","IMPRINT",EDGE,{"derivedFrom":sQuery(id+"F52.wireOp",EDGE,"E148")}),-1.0]])]});
            extrude(context, id + "F53", {"entities" : qUnion([Q0]), "operationType" : NewBodyOperationType.REMOVE, "oppositeDirection" : true, "depth" : 38.2 * mm, "offsetDistance" : 25 * mm});
        }
        {
            var Q0;
            {var subQ4=sQuery(id+"F0.wireOp",EDGE,"E11.filletArc");var subQ6=sQuery(id+"F0.wireOp",EDGE,"E9");var subQ8=sQuery(id+"F0.wireOp",EDGE,"E5");Q0=makeQuery(id+"F19.boolean.opBoolean","SPLIT",FACE,{"disambiguationData":[TD([makeQuery(id+"F1.opExtrude","SWEPT_FACE",FACE,{"disambiguationData":[OSD([subQ4])]})])],"derivedFrom":makeQuery(id+"F1.opExtrude","SWEPT_FACE",FACE,{"disambiguationData":[OSD([subQ8,subQ6])]})});}
            var sketch = newSketch(context, id + "F54", { "sketchPlane" : qUnion([Q0])});
            skLineSegment(sketch, "E157", {"start": v(-24, 109.24) * mm, "end": v(24, 109.24) * mm});
            skArc(sketch, "E158", {"start": v(-24, 104.24) * mm, "mid": v(0, 100) * mm, "end": v(24, 104.24) * mm});
            skPoint(sketch, "E159.start.orphan", {"position": v(-78.65, 78.81) * mm});
            skArc(sketch, "E160", {"start": v(-34.76, 109.24) * mm, "mid": v(0, 100) * mm, "end": v(34.76, 109.24) * mm});
            skLineSegment(sketch, "E161", {"start": v(-24, 109.24) * mm, "end": v(-34.76, 109.24) * mm});
            skLineSegment(sketch, "E162", {"start": v(24, 109.24) * mm, "end": v(34.76, 109.24) * mm});
            skLineSegment(sketch, "E163", {"start": v(-48, 98.06) * mm, "end": v(-48, 109.24) * mm});
            skLineSegment(sketch, "E164", {"start": v(-48, 109.24) * mm, "end": v(-34.76, 109.24) * mm});
            skSolve(sketch);
        }
        {
            var Q0;
            Q0 = qSketchRegion(id + "F54", true);
            extrude(context, id + "F55", {"entities" : qUnion([Q0]), "operationType" : NewBodyOperationType.REMOVE, "oppositeDirection" : true, "depth" : 49.6 * mm, "offsetDistance" : 25 * mm});
        }
        {
            var Q0;
            Q0=makeQuery(id+"F19.boolean.opBoolean","INTERSECT",EDGE,{"derivedFrom":[makeQuery(id+"F1.opExtrude","SWEPT_FACE",FACE,{"disambiguationData":[OSD([sQuery(id+"F0.wireOp",EDGE,"E5"),sQuery(id+"F0.wireOp",EDGE,"E9")])]}),makeQuery(id+"F19.opExtrude","SWEPT_FACE",FACE,{"disambiguationData":[OSD([sQuery(id+"F18.wireOp",EDGE,"E67"),sQuery(id+"F18.wireOp",EDGE,"E69")])]})]});
            var Q1;
            Q1=makeQuery(id+"F19.boolean.opBoolean","INTERSECT",EDGE,{"derivedFrom":[makeQuery(id+"F1.opExtrude","SWEPT_FACE",FACE,{"disambiguationData":[OSD([sQuery(id+"F0.wireOp",EDGE,"E5"),sQuery(id+"F0.wireOp",EDGE,"E9")])]}),makeQuery(id+"F19.opExtrude","SWEPT_FACE",FACE,{"disambiguationData":[OSD([sQuery(id+"F18.wireOp",EDGE,"E79")])]})]});
            var Q2;
            Q2=makeQuery(id+"F19.boolean.opBoolean","INTERSECT",EDGE,{"derivedFrom":[makeQuery(id+"F1.opExtrude","SWEPT_FACE",FACE,{"disambiguationData":[OSD([sQuery(id+"F0.wireOp",EDGE,"E5"),sQuery(id+"F0.wireOp",EDGE,"E9")])]}),makeQuery(id+"F19.opExtrude","SWEPT_FACE",FACE,{"disambiguationData":[OSD([sQuery(id+"F18.wireOp",EDGE,"E68")])]})]});
            var Q3;
            Q3=makeQuery(id+"F19.boolean.opBoolean","INTERSECT",EDGE,{"derivedFrom":[makeQuery(id+"F1.opExtrude","SWEPT_FACE",FACE,{"disambiguationData":[OSD([sQuery(id+"F0.wireOp",EDGE,"E5"),sQuery(id+"F0.wireOp",EDGE,"E9")])]}),makeQuery(id+"F19.opExtrude","SWEPT_FACE",FACE,{"disambiguationData":[OSD([sQuery(id+"F18.wireOp",EDGE,"E80.MirrorCS")])]})]});
            var Q4;
            Q4=makeQuery(id+"F19.boolean.opBoolean","COPY",EDGE,{"derivedFrom":makeQuery(id+"F19.opExtrude","CAP_EDGE",EDGE,{"disambiguationData":[OSD([sQuery(id+"F18.wireOp",EDGE,"E82")])],"isStart":true})});
            var Q5;
            Q5=makeQuery(id+"F19.boolean.opBoolean","COPY",EDGE,{"derivedFrom":makeQuery(id+"F19.opExtrude","CAP_EDGE",EDGE,{"disambiguationData":[OSD([sQuery(id+"F18.wireOp",EDGE,"E81")])],"isStart":true})});
            fillet(context, id + "F56", {"entities" : qUnion([Q0, Q1, Q2, Q3, Q4, Q5]), "radius" : 1 * mm, "tangentPropagation" : true, "allowEdgeOverflow" : false});
        }
        {
            var Q0;
            Q0=makeQuery(id+"F53.boolean.opBoolean","COPY",FACE,{"derivedFrom":makeQuery(id+"F53.opExtrude","SWEPT_FACE",FACE,{"disambiguationData":[OSD([sQuery(id+"F52.wireOp",EDGE,"E150")])]})});
            var Q1;
            Q1=makeQuery(id+"F55.boolean.opBoolean","COPY",FACE,{"derivedFrom":makeQuery(id+"F55.opExtrude","SWEPT_FACE",FACE,{"disambiguationData":[OSD([sQuery(id+"F54.wireOp",EDGE,"E160")])]})});
            fillet(context, id + "F57", {"entities" : qUnion([Q0, Q1]), "radius" : 2.5 * mm, "tangentPropagation" : true, "allowEdgeOverflow" : false});
        }
        {
            var Q0;
            Q0=makeQuery(id+"F44.boolean.opBoolean","INTERSECT",EDGE,{"derivedFrom":[makeQuery(id+"F1.opExtrude","SWEPT_FACE",FACE,{"disambiguationData":[OSD([sQuery(id+"F0.wireOp",EDGE,"E10.MirrorCS"),sQuery(id+"F0.wireOp",EDGE,"E13")])]}),makeQuery(id+"F44.opExtrude","SWEPT_FACE",FACE,{"disambiguationData":[OSD([sQuery(id+"F43.wireOp",EDGE,"E145")])]})]});
            var Q1;
            Q1=makeQuery(id+"F44.boolean.opBoolean","INTERSECT",EDGE,{"derivedFrom":[makeQuery(id+"F1.opExtrude","SWEPT_FACE",FACE,{"disambiguationData":[OSD([sQuery(id+"F0.wireOp",EDGE,"E10.MirrorCS"),sQuery(id+"F0.wireOp",EDGE,"E13")])]}),makeQuery(id+"F44.opExtrude","CAP_FACE",FACE,{"disambiguationData":[OSD([sQuery(id+"F43.wireOp",EDGE,"E144"),sQuery(id+"F43.wireOp",EDGE,"E145"),sQuery(id+"F43.wireOp",EDGE,"E146"),sQuery(id+"F43.wireOp",EDGE,"E147")])],"isStart":true})]});
            var Q2;
            Q2=makeQuery(id+"F44.boolean.opBoolean","INTERSECT",EDGE,{"derivedFrom":[makeQuery(id+"F1.opExtrude","SWEPT_FACE",FACE,{"disambiguationData":[OSD([sQuery(id+"F0.wireOp",EDGE,"E10.MirrorCS"),sQuery(id+"F0.wireOp",EDGE,"E13")])]}),makeQuery(id+"F44.opExtrude","SWEPT_FACE",FACE,{"disambiguationData":[OSD([sQuery(id+"F43.wireOp",EDGE,"E144")])]})]});
            var Q3;
            Q3=makeQuery(id+"F44.boolean.opBoolean","INTERSECT",EDGE,{"derivedFrom":[makeQuery(id+"F1.opExtrude","SWEPT_FACE",FACE,{"disambiguationData":[OSD([sQuery(id+"F0.wireOp",EDGE,"E10.MirrorCS"),sQuery(id+"F0.wireOp",EDGE,"E13")])]}),makeQuery(id+"F44.opExtrude","CAP_FACE",FACE,{"disambiguationData":[OSD([sQuery(id+"F43.wireOp",EDGE,"E144"),sQuery(id+"F43.wireOp",EDGE,"E145"),sQuery(id+"F43.wireOp",EDGE,"E146"),sQuery(id+"F43.wireOp",EDGE,"E147")])],"isStart":false})]});
            var Q4;
            {var subQ40=sQuery(id+"F43.wireOp",EDGE,"E145");Q4=makeQuery(id+"F48.boolean.opBoolean","INTERSECT",EDGE,{"derivedFrom":[makeQuery(id+"F44.boolean.opBoolean","COPY",FACE,{"disambiguationData":[TD([makeQuery(id+"F25.boolean.opBoolean","COPY",FACE,{"derivedFrom":makeQuery(id+"F25.opExtrude","SWEPT_FACE",FACE,{"disambiguationData":[OSD([sQuery(id+"F24.wireOp",EDGE,"E97.sketch_text.stroke-0")])]})})])],"derivedFrom":makeQuery(id+"F44.opExtrude","SWEPT_FACE",FACE,{"disambiguationData":[OSD([subQ40])]})}),makeQuery(id+"F48.opExtrude","SWEPT_FACE",FACE,{"disambiguationData":[OSD([sQuery(id+"F22.wireOp",EDGE,"E95.MirrorCS")])]})]});}
            var Q5;
            {var subQ40=sQuery(id+"F43.wireOp",EDGE,"E145");Q5=makeQuery(id+"F48.boolean.opBoolean","INTERSECT",EDGE,{"derivedFrom":[makeQuery(id+"F44.boolean.opBoolean","COPY",FACE,{"disambiguationData":[TD([makeQuery(id+"F25.boolean.opBoolean","COPY",FACE,{"derivedFrom":makeQuery(id+"F25.opExtrude","SWEPT_FACE",FACE,{"disambiguationData":[OSD([sQuery(id+"F24.wireOp",EDGE,"E97.sketch_text.stroke-0")])]})})])],"derivedFrom":makeQuery(id+"F44.opExtrude","SWEPT_FACE",FACE,{"disambiguationData":[OSD([subQ40])]})}),makeQuery(id+"F48.opExtrude","SWEPT_FACE",FACE,{"disambiguationData":[OSD([sQuery(id+"F22.wireOp",EDGE,"E93")])]})]});}
            var Q6;
            {var subQ4=sQuery(id+"F0.wireOp",EDGE,"E11.filletArc");var subQ6=sQuery(id+"F0.wireOp",EDGE,"E9");var subQ8=sQuery(id+"F0.wireOp",EDGE,"E5");Q6=makeQuery(id+"F44.boolean.opBoolean","INTERSECT",EDGE,{"derivedFrom":[makeQuery(id+"F19.boolean.opBoolean","SPLIT",FACE,{"disambiguationData":[TD([makeQuery(id+"F1.opExtrude","SWEPT_FACE",FACE,{"disambiguationData":[OSD([subQ4])]})])],"derivedFrom":makeQuery(id+"F1.opExtrude","SWEPT_FACE",FACE,{"disambiguationData":[OSD([subQ8,subQ6])]})}),makeQuery(id+"F44.opExtrude","SWEPT_FACE",FACE,{"disambiguationData":[OSD([sQuery(id+"F43.wireOp",EDGE,"E145")])]})]});}
            var Q7;
            {var subQ4=sQuery(id+"F0.wireOp",EDGE,"E11.filletArc");var subQ6=sQuery(id+"F0.wireOp",EDGE,"E9");var subQ8=sQuery(id+"F0.wireOp",EDGE,"E5");Q7=makeQuery(id+"F44.boolean.opBoolean","INTERSECT",EDGE,{"derivedFrom":[makeQuery(id+"F19.boolean.opBoolean","SPLIT",FACE,{"disambiguationData":[TD([makeQuery(id+"F1.opExtrude","SWEPT_FACE",FACE,{"disambiguationData":[OSD([subQ4])]})])],"derivedFrom":makeQuery(id+"F1.opExtrude","SWEPT_FACE",FACE,{"disambiguationData":[OSD([subQ8,subQ6])]})}),makeQuery(id+"F44.opExtrude","CAP_FACE",FACE,{"disambiguationData":[OSD([sQuery(id+"F43.wireOp",EDGE,"E144"),sQuery(id+"F43.wireOp",EDGE,"E145"),sQuery(id+"F43.wireOp",EDGE,"E146"),sQuery(id+"F43.wireOp",EDGE,"E147")])],"isStart":false})]});}
            var Q8;
            {var subQ4=sQuery(id+"F0.wireOp",EDGE,"E11.filletArc");var subQ6=sQuery(id+"F0.wireOp",EDGE,"E9");var subQ8=sQuery(id+"F0.wireOp",EDGE,"E5");Q8=makeQuery(id+"F44.boolean.opBoolean","INTERSECT",EDGE,{"derivedFrom":[makeQuery(id+"F19.boolean.opBoolean","SPLIT",FACE,{"disambiguationData":[TD([makeQuery(id+"F1.opExtrude","SWEPT_FACE",FACE,{"disambiguationData":[OSD([subQ4])]})])],"derivedFrom":makeQuery(id+"F1.opExtrude","SWEPT_FACE",FACE,{"disambiguationData":[OSD([subQ8,subQ6])]})}),makeQuery(id+"F44.opExtrude","SWEPT_FACE",FACE,{"disambiguationData":[OSD([sQuery(id+"F43.wireOp",EDGE,"E144")])]})]});}
            var Q9;
            {var subQ4=sQuery(id+"F0.wireOp",EDGE,"E11.filletArc");var subQ6=sQuery(id+"F0.wireOp",EDGE,"E9");var subQ8=sQuery(id+"F0.wireOp",EDGE,"E5");Q9=makeQuery(id+"F44.boolean.opBoolean","INTERSECT",EDGE,{"derivedFrom":[makeQuery(id+"F19.boolean.opBoolean","SPLIT",FACE,{"disambiguationData":[TD([makeQuery(id+"F1.opExtrude","SWEPT_FACE",FACE,{"disambiguationData":[OSD([subQ4])]})])],"derivedFrom":makeQuery(id+"F1.opExtrude","SWEPT_FACE",FACE,{"disambiguationData":[OSD([subQ8,subQ6])]})}),makeQuery(id+"F44.opExtrude","CAP_FACE",FACE,{"disambiguationData":[OSD([sQuery(id+"F43.wireOp",EDGE,"E144"),sQuery(id+"F43.wireOp",EDGE,"E145"),sQuery(id+"F43.wireOp",EDGE,"E146"),sQuery(id+"F43.wireOp",EDGE,"E147")])],"isStart":true})]});}
            fillet(context, id + "F58", {"entities" : qUnion([Q0, Q1, Q2, Q3, Q4, Q5, Q6, Q7, Q8, Q9]), "radius" : 3 * mm, "tangentPropagation" : true, "allowEdgeOverflow" : false});
        }
        {
            var Q0;
            Q0=makeQuery(id+"F48.boolean.opBoolean","INTERSECT",EDGE,{"derivedFrom":[makeQuery(id+"F21.boolean.opBoolean","COPY",FACE,{"derivedFrom":makeQuery(id+"F21.opExtrude","SWEPT_FACE",FACE,{"disambiguationData":[OSD([sQuery(id+"F18.wireOp",EDGE,"E71.3")])]})}),makeQuery(id+"F48.opExtrude","SWEPT_FACE",FACE,{"disambiguationData":[OSD([sQuery(id+"F22.wireOp",EDGE,"E93")])]})]});
            var Q1;
            Q1=makeQuery(id+"F48.boolean.opBoolean","INTERSECT",EDGE,{"derivedFrom":[makeQuery(id+"F21.boolean.opBoolean","COPY",FACE,{"derivedFrom":makeQuery(id+"F21.opExtrude","SWEPT_FACE",FACE,{"disambiguationData":[OSD([sQuery(id+"F18.wireOp",EDGE,"E71.2")])]})}),makeQuery(id+"F48.opExtrude","SWEPT_FACE",FACE,{"disambiguationData":[OSD([sQuery(id+"F22.wireOp",EDGE,"E93")])]})]});
            var Q2;
            Q2=makeQuery(id+"F48.boolean.opBoolean","INTERSECT",EDGE,{"derivedFrom":[makeQuery(id+"F21.boolean.opBoolean","COPY",FACE,{"derivedFrom":makeQuery(id+"F21.opExtrude","SWEPT_FACE",FACE,{"disambiguationData":[OSD([sQuery(id+"F18.wireOp",EDGE,"E71.1")])]})}),makeQuery(id+"F48.opExtrude","SWEPT_FACE",FACE,{"disambiguationData":[OSD([sQuery(id+"F22.wireOp",EDGE,"E93")])]})]});
            var Q3;
            Q3=makeQuery(id+"F48.boolean.opBoolean","INTERSECT",EDGE,{"derivedFrom":[makeQuery(id+"F21.boolean.opBoolean","COPY",FACE,{"derivedFrom":makeQuery(id+"F21.opExtrude","SWEPT_FACE",FACE,{"disambiguationData":[OSD([sQuery(id+"F18.wireOp",EDGE,"E71.0")])]})}),makeQuery(id+"F48.opExtrude","SWEPT_FACE",FACE,{"disambiguationData":[OSD([sQuery(id+"F22.wireOp",EDGE,"E93")])]})]});
            var Q4;
            Q4=makeQuery(id+"F48.boolean.opBoolean","INTERSECT",EDGE,{"derivedFrom":[makeQuery(id+"F21.boolean.opBoolean","COPY",FACE,{"derivedFrom":makeQuery(id+"F21.opExtrude","SWEPT_FACE",FACE,{"disambiguationData":[OSD([sQuery(id+"F18.wireOp",EDGE,"E71.5")])]})}),makeQuery(id+"F48.opExtrude","SWEPT_FACE",FACE,{"disambiguationData":[OSD([sQuery(id+"F22.wireOp",EDGE,"E93")])]})]});
            var Q5;
            Q5=makeQuery(id+"F48.boolean.opBoolean","INTERSECT",EDGE,{"derivedFrom":[makeQuery(id+"F21.boolean.opBoolean","COPY",FACE,{"derivedFrom":makeQuery(id+"F21.opExtrude","SWEPT_FACE",FACE,{"disambiguationData":[OSD([sQuery(id+"F18.wireOp",EDGE,"E71.4")])]})}),makeQuery(id+"F48.opExtrude","SWEPT_FACE",FACE,{"disambiguationData":[OSD([sQuery(id+"F22.wireOp",EDGE,"E93")])]})]});
            var Q6;
            Q6=makeQuery(id+"F48.boolean.opBoolean","INTERSECT",EDGE,{"derivedFrom":[makeQuery(id+"F21.boolean.opBoolean","COPY",FACE,{"derivedFrom":makeQuery(id+"F21.opExtrude","SWEPT_FACE",FACE,{"disambiguationData":[OSD([sQuery(id+"F18.wireOp",EDGE,"E72.MirrorCS")])]})}),makeQuery(id+"F48.opExtrude","SWEPT_FACE",FACE,{"disambiguationData":[OSD([sQuery(id+"F22.wireOp",EDGE,"E93")])]})]});
            var Q7;
            Q7=makeQuery(id+"F48.boolean.opBoolean","INTERSECT",EDGE,{"derivedFrom":[makeQuery(id+"F21.boolean.opBoolean","COPY",FACE,{"derivedFrom":makeQuery(id+"F21.opExtrude","SWEPT_FACE",FACE,{"disambiguationData":[OSD([sQuery(id+"F18.wireOp",EDGE,"E73.MirrorCS")])]})}),makeQuery(id+"F48.opExtrude","SWEPT_FACE",FACE,{"disambiguationData":[OSD([sQuery(id+"F22.wireOp",EDGE,"E93")])]})]});
            var Q8;
            Q8=makeQuery(id+"F48.boolean.opBoolean","INTERSECT",EDGE,{"derivedFrom":[makeQuery(id+"F21.boolean.opBoolean","COPY",FACE,{"derivedFrom":makeQuery(id+"F21.opExtrude","SWEPT_FACE",FACE,{"disambiguationData":[OSD([sQuery(id+"F18.wireOp",EDGE,"E74.MirrorCS")])]})}),makeQuery(id+"F48.opExtrude","SWEPT_FACE",FACE,{"disambiguationData":[OSD([sQuery(id+"F22.wireOp",EDGE,"E93")])]})]});
            var Q9;
            Q9=makeQuery(id+"F48.boolean.opBoolean","INTERSECT",EDGE,{"derivedFrom":[makeQuery(id+"F21.boolean.opBoolean","COPY",FACE,{"derivedFrom":makeQuery(id+"F21.opExtrude","SWEPT_FACE",FACE,{"disambiguationData":[OSD([sQuery(id+"F18.wireOp",EDGE,"E75.MirrorCS")])]})}),makeQuery(id+"F48.opExtrude","SWEPT_FACE",FACE,{"disambiguationData":[OSD([sQuery(id+"F22.wireOp",EDGE,"E93")])]})]});
            var Q10;
            Q10=makeQuery(id+"F48.boolean.opBoolean","INTERSECT",EDGE,{"derivedFrom":[makeQuery(id+"F21.boolean.opBoolean","COPY",FACE,{"derivedFrom":makeQuery(id+"F21.opExtrude","SWEPT_FACE",FACE,{"disambiguationData":[OSD([sQuery(id+"F18.wireOp",EDGE,"E76.MirrorCS")])]})}),makeQuery(id+"F48.opExtrude","SWEPT_FACE",FACE,{"disambiguationData":[OSD([sQuery(id+"F22.wireOp",EDGE,"E93")])]})]});
            var Q11;
            Q11=makeQuery(id+"F48.boolean.opBoolean","INTERSECT",EDGE,{"derivedFrom":[makeQuery(id+"F21.boolean.opBoolean","COPY",FACE,{"derivedFrom":makeQuery(id+"F21.opExtrude","SWEPT_FACE",FACE,{"disambiguationData":[OSD([sQuery(id+"F18.wireOp",EDGE,"E77.MirrorCS")])]})}),makeQuery(id+"F48.opExtrude","SWEPT_FACE",FACE,{"disambiguationData":[OSD([sQuery(id+"F22.wireOp",EDGE,"E93")])]})]});
            fillet(context, id + "F59", {"entities" : qUnion([Q0, Q1, Q2, Q3, Q4, Q5, Q6, Q7, Q8, Q9, Q10, Q11]), "radius" : 1 * mm, "tangentPropagation" : true, "allowEdgeOverflow" : false});
        }
        {
            var Q0;
            Q0=makeQuery(id+"F48.boolean.opBoolean","INTERSECT",EDGE,{"derivedFrom":[makeQuery(id+"F41.boolean.opBoolean","COPY",FACE,{"derivedFrom":makeQuery(id+"F41.opExtrude","SWEPT_FACE",FACE,{"disambiguationData":[OSD([sQuery(id+"F39.wireOp",EDGE,"E129.MirrorCS")])]})}),makeQuery(id+"F48.opExtrude","SWEPT_FACE",FACE,{"disambiguationData":[OSD([sQuery(id+"F22.wireOp",EDGE,"E85"),sQuery(id+"F22.wireOp",EDGE,"E88.MirrorCS")])]})]});
            var Q1;
            Q1=makeQuery(id+"F48.boolean.opBoolean","INTERSECT",EDGE,{"derivedFrom":[makeQuery(id+"F41.boolean.opBoolean","COPY",FACE,{"derivedFrom":makeQuery(id+"F41.opExtrude","SWEPT_FACE",FACE,{"disambiguationData":[OSD([sQuery(id+"F39.wireOp",EDGE,"E130.MirrorCS")])]})}),makeQuery(id+"F48.opExtrude","SWEPT_FACE",FACE,{"disambiguationData":[OSD([sQuery(id+"F22.wireOp",EDGE,"E85"),sQuery(id+"F22.wireOp",EDGE,"E88.MirrorCS")])]})]});
            var Q2;
            Q2=makeQuery(id+"F41.boolean.opBoolean","COPY",EDGE,{"derivedFrom":makeQuery(id+"F41.opExtrude","SWEPT_EDGE",EDGE,{"disambiguationData":[OSD([sQuery(id+"F39.wireOp",EDGE,"E130.MirrorCS"),sQuery(id+"F39.wireOp",EDGE,"E131.MirrorCS")])]})});
            var Q3;
            Q3=makeQuery(id+"F48.boolean.opBoolean","INTERSECT",EDGE,{"derivedFrom":[makeQuery(id+"F41.boolean.opBoolean","COPY",FACE,{"derivedFrom":makeQuery(id+"F41.opExtrude","SWEPT_FACE",FACE,{"disambiguationData":[OSD([sQuery(id+"F39.wireOp",EDGE,"E133.MirrorCS")])]})}),makeQuery(id+"F48.opExtrude","SWEPT_FACE",FACE,{"disambiguationData":[OSD([sQuery(id+"F22.wireOp",EDGE,"E85"),sQuery(id+"F22.wireOp",EDGE,"E88.MirrorCS")])]})]});
            var Q4;
            Q4=makeQuery(id+"F48.boolean.opBoolean","INTERSECT",EDGE,{"derivedFrom":[makeQuery(id+"F41.boolean.opBoolean","COPY",FACE,{"derivedFrom":makeQuery(id+"F41.opExtrude","SWEPT_FACE",FACE,{"disambiguationData":[OSD([sQuery(id+"F39.wireOp",EDGE,"E131.MirrorCS")])]})}),makeQuery(id+"F48.opExtrude","SWEPT_FACE",FACE,{"disambiguationData":[OSD([sQuery(id+"F22.wireOp",EDGE,"E85"),sQuery(id+"F22.wireOp",EDGE,"E88.MirrorCS")])]})]});
            var Q5;
            Q5=makeQuery(id+"F50.opFillet","BLEND_EDGE",EDGE,{"blendedFrom":[makeQuery(id+"F48.boolean.opBoolean","INTERSECT",EDGE,{"derivedFrom":[makeQuery(id+"F23.boolean.opBoolean","COPY",FACE,{"derivedFrom":makeQuery(id+"F23.opExtrude","CAP_FACE",FACE,{"disambiguationData":[OSD([sQuery(id+"F22.wireOp",EDGE,"E90"),sQuery(id+"F22.wireOp",EDGE,"E91.MirrorCS"),sQuery(id+"F22.wireOp",EDGE,"E93"),sQuery(id+"F22.wireOp",EDGE,"E94"),sQuery(id+"F22.wireOp",EDGE,"E95.MirrorCS"),sQuery(id+"F22.wireOp",EDGE,"E96.MirrorCS")])],"isStart":true})}),makeQuery(id+"F48.opExtrude","SWEPT_FACE",FACE,{"disambiguationData":[OSD([sQuery(id+"F22.wireOp",EDGE,"E85"),sQuery(id+"F22.wireOp",EDGE,"E88.MirrorCS")])]})]}),makeQuery(id+"F41.boolean.opBoolean","COPY",FACE,{"derivedFrom":makeQuery(id+"F41.opExtrude","SWEPT_FACE",FACE,{"disambiguationData":[OSD([sQuery(id+"F39.wireOp",EDGE,"E132.MirrorCS")])]})})],"blendedInto":[makeQuery(id+"F41.boolean.opBoolean","COPY",FACE,{"derivedFrom":makeQuery(id+"F41.opExtrude","SWEPT_FACE",FACE,{"disambiguationData":[OSD([sQuery(id+"F39.wireOp",EDGE,"E132.MirrorCS")])]})})]});
            var Q6;
            Q6=makeQuery(id+"F48.boolean.opBoolean","INTERSECT",EDGE,{"derivedFrom":[makeQuery(id+"F41.boolean.opBoolean","COPY",FACE,{"derivedFrom":makeQuery(id+"F41.opExtrude","SWEPT_FACE",FACE,{"disambiguationData":[OSD([sQuery(id+"F39.wireOp",EDGE,"E134.MirrorCS")])]})}),makeQuery(id+"F48.opExtrude","SWEPT_FACE",FACE,{"disambiguationData":[OSD([sQuery(id+"F22.wireOp",EDGE,"E85"),sQuery(id+"F22.wireOp",EDGE,"E88.MirrorCS")])]})]});
            var Q7;
            Q7=makeQuery(id+"F48.boolean.opBoolean","INTERSECT",EDGE,{"derivedFrom":[makeQuery(id+"F41.boolean.opBoolean","COPY",FACE,{"derivedFrom":makeQuery(id+"F41.opExtrude","SWEPT_FACE",FACE,{"disambiguationData":[OSD([sQuery(id+"F39.wireOp",EDGE,"E128.3")])]})}),makeQuery(id+"F48.opExtrude","SWEPT_FACE",FACE,{"disambiguationData":[OSD([sQuery(id+"F22.wireOp",EDGE,"E85"),sQuery(id+"F22.wireOp",EDGE,"E88.MirrorCS")])]})]});
            var Q8;
            Q8=makeQuery(id+"F48.boolean.opBoolean","INTERSECT",EDGE,{"derivedFrom":[makeQuery(id+"F41.boolean.opBoolean","COPY",FACE,{"derivedFrom":makeQuery(id+"F41.opExtrude","SWEPT_FACE",FACE,{"disambiguationData":[OSD([sQuery(id+"F39.wireOp",EDGE,"E128.4")])]})}),makeQuery(id+"F48.opExtrude","SWEPT_FACE",FACE,{"disambiguationData":[OSD([sQuery(id+"F22.wireOp",EDGE,"E85"),sQuery(id+"F22.wireOp",EDGE,"E88.MirrorCS")])]})]});
            var Q9;
            Q9=makeQuery(id+"F48.boolean.opBoolean","INTERSECT",EDGE,{"derivedFrom":[makeQuery(id+"F41.boolean.opBoolean","COPY",FACE,{"derivedFrom":makeQuery(id+"F41.opExtrude","SWEPT_FACE",FACE,{"disambiguationData":[OSD([sQuery(id+"F39.wireOp",EDGE,"E128.5")])]})}),makeQuery(id+"F48.opExtrude","SWEPT_FACE",FACE,{"disambiguationData":[OSD([sQuery(id+"F22.wireOp",EDGE,"E85"),sQuery(id+"F22.wireOp",EDGE,"E88.MirrorCS")])]})]});
            var Q10;
            Q10=makeQuery(id+"F48.boolean.opBoolean","INTERSECT",EDGE,{"derivedFrom":[makeQuery(id+"F41.boolean.opBoolean","COPY",FACE,{"derivedFrom":makeQuery(id+"F41.opExtrude","SWEPT_FACE",FACE,{"disambiguationData":[OSD([sQuery(id+"F39.wireOp",EDGE,"E128.1")])]})}),makeQuery(id+"F48.opExtrude","SWEPT_FACE",FACE,{"disambiguationData":[OSD([sQuery(id+"F22.wireOp",EDGE,"E85"),sQuery(id+"F22.wireOp",EDGE,"E88.MirrorCS")])]})]});
            var Q11;
            Q11=makeQuery(id+"F48.boolean.opBoolean","INTERSECT",EDGE,{"derivedFrom":[makeQuery(id+"F41.boolean.opBoolean","COPY",FACE,{"derivedFrom":makeQuery(id+"F41.opExtrude","SWEPT_FACE",FACE,{"disambiguationData":[OSD([sQuery(id+"F39.wireOp",EDGE,"E128.2")])]})}),makeQuery(id+"F48.opExtrude","SWEPT_FACE",FACE,{"disambiguationData":[OSD([sQuery(id+"F22.wireOp",EDGE,"E85"),sQuery(id+"F22.wireOp",EDGE,"E88.MirrorCS")])]})]});
            var Q12;
            Q12=makeQuery(id+"F50.opFillet","BLEND_EDGE",EDGE,{"blendedFrom":[makeQuery(id+"F48.boolean.opBoolean","INTERSECT",EDGE,{"derivedFrom":[makeQuery(id+"F23.boolean.opBoolean","COPY",FACE,{"derivedFrom":makeQuery(id+"F23.opExtrude","CAP_FACE",FACE,{"disambiguationData":[OSD([sQuery(id+"F22.wireOp",EDGE,"E90"),sQuery(id+"F22.wireOp",EDGE,"E91.MirrorCS"),sQuery(id+"F22.wireOp",EDGE,"E93"),sQuery(id+"F22.wireOp",EDGE,"E94"),sQuery(id+"F22.wireOp",EDGE,"E95.MirrorCS"),sQuery(id+"F22.wireOp",EDGE,"E96.MirrorCS")])],"isStart":true})}),makeQuery(id+"F48.opExtrude","SWEPT_FACE",FACE,{"disambiguationData":[OSD([sQuery(id+"F22.wireOp",EDGE,"E85"),sQuery(id+"F22.wireOp",EDGE,"E88.MirrorCS")])]})]}),makeQuery(id+"F41.boolean.opBoolean","COPY",FACE,{"derivedFrom":makeQuery(id+"F41.opExtrude","SWEPT_FACE",FACE,{"disambiguationData":[OSD([sQuery(id+"F39.wireOp",EDGE,"E128.0")])]})})],"blendedInto":[makeQuery(id+"F41.boolean.opBoolean","COPY",FACE,{"derivedFrom":makeQuery(id+"F41.opExtrude","SWEPT_FACE",FACE,{"disambiguationData":[OSD([sQuery(id+"F39.wireOp",EDGE,"E128.0")])]})})]});
            fillet(context, id + "F60", {"entities" : qUnion([Q0, Q1, Q2, Q3, Q4, Q5, Q6, Q7, Q8, Q9, Q10, Q11, Q12]), "radius" : 1 * mm, "tangentPropagation" : true, "allowEdgeOverflow" : false});
        }
        {
            var Q0;
            Q0=qCreatedBy(makeId("Top.planeOp"),FACE);
            var sketch = newSketch(context, id + "F61", { "sketchPlane" : qUnion([Q0])});
            skLineSegment(sketch, "E165", {"start": v(0, 0) * mm, "end": v(-57, 0) * mm});
            skLineSegment(sketch, "E166", {"start": v(-57, 0) * mm, "end": v(-57, 55) * mm});
            skLineSegment(sketch, "E167", {"start": v(0, 55) * mm, "end": v(0, -46.1) * mm, "construction": true});
            skLineSegment(sketch, "E168", {"start": v(0, 0) * mm, "end": v(-33.21, 0) * mm, "construction": true});
            skLineSegment(sketch, "E169.MirrorCS", {"start": v(57, 0) * mm, "end": v(57, 55) * mm});
            skLineSegment(sketch, "E170.MirrorCS", {"start": v(0, 0) * mm, "end": v(33.21, 0) * mm, "construction": true});
            skLineSegment(sketch, "E171.MirrorCS", {"start": v(-57, 0) * mm, "end": v(-57, -55) * mm});
            skLineSegment(sketch, "E172.MirrorCS", {"start": v(-57, -55) * mm, "end": v(0, -55) * mm});
            skLineSegment(sketch, "E173.MirrorCS", {"start": v(57, -55) * mm, "end": v(0, -55) * mm});
            skLineSegment(sketch, "E174.MirrorCS", {"start": v(57, 0) * mm, "end": v(57, -55) * mm});
            skArc(sketch, "E175", {"start": v(-60, -20.8) * mm, "mid": v(-50.5, 0) * mm, "end": v(-60, 20.8) * mm});
            skLineSegment(sketch, "E176", {"start": v(-60, 20.8) * mm, "end": v(-60, -20.8) * mm});
            skLineSegment(sketch, "E177.1.0.0", {"start": v(0, 20.8) * mm, "end": v(0, -20.8) * mm});
            skArc(sketch, "E177.1.0.1", {"start": v(-20, 60) * mm, "mid": v(0.8, 50.5) * mm, "end": v(21.58, 60) * mm});
            skLineSegment(sketch, "E177.direction1", {"start": v(-60, -20.8) * mm, "end": v(0, -20.8) * mm, "construction": true});
            skLineSegment(sketch, "E178", {"start": v(-20, 55) * mm, "end": v(21.58, 55) * mm});
            skLineSegment(sketch, "E179", {"start": v(-57, 55) * mm, "end": v(57, 55) * mm});
            skLineSegment(sketch, "E180", {"start": v(-20, 60) * mm, "end": v(21.58, 60) * mm});
            skLineSegment(sketch, "E181", {"start": v(-60, 20.8) * mm, "end": v(-60, 30.8) * mm});
            skLineSegment(sketch, "E182", {"start": v(-60, -20.8) * mm, "end": v(-60, -30.8) * mm});
            skArc(sketch, "E183", {"start": v(-60, -30.8) * mm, "mid": v(-50.05, 0) * mm, "end": v(-60, 30.8) * mm});
            skLineSegment(sketch, "E184", {"start": v(-20, 60) * mm, "end": v(-30, 60) * mm});
            skLineSegment(sketch, "E185", {"start": v(21.58, 60) * mm, "end": v(31.58, 60) * mm});
            skArc(sketch, "E186", {"start": v(-30, 60) * mm, "mid": v(0.8, 49.98) * mm, "end": v(31.58, 60) * mm});
            skSolve(sketch);
        }
        {
            var Q0;
            {var subQ3=sQuery(id+"F61.wireOp",EDGE,"E176");Q0=makeQuery(id+"F61.imprint","IMPRINT",FACE,{"disambiguationData":[TD([[makeQuery(id+"F61.imprint","IMPRINT",EDGE,{"derivedFrom":subQ3}),1.0]])]});}
            var Q1;
            {var subQ0=sQuery(id+"F61.wireOp",EDGE,"E175");var subQ1=sQuery(id+"F61.wireOp",EDGE,"E165");var subQ2=makeQuery(id+"F61.imprint","INTERSECT",VERTEX,{"derivedFrom":[subQ1,subQ0]});Q1=makeQuery(id+"F61.imprint","IMPRINT",FACE,{"disambiguationData":[TD([[makeQuery(id+"F61.imprint","IMPRINT",EDGE,{"disambiguationData":[TD([[subQ2,-1.0]])],"derivedFrom":subQ0}),1.0]])]});}
            var Q2;
            {var subQ0=sQuery(id+"F61.wireOp",EDGE,"E175");var subQ1=sQuery(id+"F61.wireOp",EDGE,"E165");var subQ2=makeQuery(id+"F61.imprint","INTERSECT",VERTEX,{"derivedFrom":[subQ1,subQ0]});Q2=makeQuery(id+"F61.imprint","IMPRINT",FACE,{"disambiguationData":[TD([[makeQuery(id+"F61.imprint","IMPRINT",EDGE,{"disambiguationData":[TD([[subQ2,1.0]])],"derivedFrom":subQ0}),1.0]])]});}
            var Q3;
            {var subQ0=sQuery(id+"F61.wireOp",EDGE,"E180");Q3=makeQuery(id+"F61.imprint","IMPRINT",FACE,{"disambiguationData":[TD([[makeQuery(id+"F61.imprint","IMPRINT",EDGE,{"derivedFrom":subQ0}),-1.0]])]});}
            var Q4;
            {var subQ0=sQuery(id+"F61.wireOp",EDGE,"E178");var subQ1=sQuery(id+"F61.wireOp",EDGE,"E177.1.0.1");var subQ2=makeQuery(id+"F61.imprint","INTERSECT",VERTEX,{"disambiguationData":[OD(0.0)],"derivedFrom":[subQ1,subQ0]});Q4=makeQuery(id+"F61.imprint","IMPRINT",FACE,{"disambiguationData":[TD([[makeQuery(id+"F61.imprint","IMPRINT",EDGE,{"disambiguationData":[TD([[subQ2,-1.0]])],"derivedFrom":subQ1}),1.0]])]});}
            var Q5;
            {var subQ0=sQuery(id+"F61.wireOp",EDGE,"E184");Q5=makeQuery(id+"F61.imprint","IMPRINT",FACE,{"disambiguationData":[TD([[makeQuery(id+"F61.imprint","IMPRINT",EDGE,{"derivedFrom":subQ0}),1.0]])]});}
            var Q6;
            {var subQ1=sQuery(id+"F61.wireOp",EDGE,"E178");var subQ5=sQuery(id+"F61.wireOp",EDGE,"E177.1.0.1");var subQ7=makeQuery(id+"F61.imprint","INTERSECT",VERTEX,{"disambiguationData":[OD(0.0)],"derivedFrom":[subQ5,subQ1]});Q6=makeQuery(id+"F61.imprint","IMPRINT",FACE,{"disambiguationData":[TD([[makeQuery(id+"F61.imprint","IMPRINT",EDGE,{"disambiguationData":[TD([[subQ7,-1.0]])],"derivedFrom":subQ5}),-1.0]])]});}
            var Q7;
            {var subQ0=sQuery(id+"F61.wireOp",EDGE,"E185");Q7=makeQuery(id+"F61.imprint","IMPRINT",FACE,{"disambiguationData":[TD([[makeQuery(id+"F61.imprint","IMPRINT",EDGE,{"derivedFrom":subQ0}),-1.0]])]});}
            var Q8;
            {var subQ0=sQuery(id+"F61.wireOp",EDGE,"E175");var subQ1=sQuery(id+"F61.wireOp",EDGE,"E165");var subQ2=makeQuery(id+"F61.imprint","INTERSECT",VERTEX,{"derivedFrom":[subQ1,subQ0]});Q8=makeQuery(id+"F61.imprint","IMPRINT",FACE,{"disambiguationData":[TD([[makeQuery(id+"F61.imprint","IMPRINT",EDGE,{"disambiguationData":[TD([[subQ2,1.0]])],"derivedFrom":subQ1}),1.0]])]});}
            var Q9;
            {var subQ5=sQuery(id+"F61.wireOp",EDGE,"E182");Q9=makeQuery(id+"F61.imprint","IMPRINT",FACE,{"disambiguationData":[TD([[makeQuery(id+"F61.imprint","IMPRINT",EDGE,{"derivedFrom":subQ5}),1.0]])]});}
            var Q10;
            {var subQ0=sQuery(id+"F61.wireOp",EDGE,"E175");var subQ1=sQuery(id+"F61.wireOp",EDGE,"E165");var subQ2=makeQuery(id+"F61.imprint","INTERSECT",VERTEX,{"derivedFrom":[subQ1,subQ0]});Q10=makeQuery(id+"F61.imprint","IMPRINT",FACE,{"disambiguationData":[TD([[makeQuery(id+"F61.imprint","IMPRINT",EDGE,{"disambiguationData":[TD([[subQ2,1.0]])],"derivedFrom":subQ1}),-1.0]])]});}
            var Q11;
            {var subQ5=sQuery(id+"F61.wireOp",EDGE,"E181");Q11=makeQuery(id+"F61.imprint","IMPRINT",FACE,{"disambiguationData":[TD([[makeQuery(id+"F61.imprint","IMPRINT",EDGE,{"derivedFrom":subQ5}),-1.0]])]});}
            extrude(context, id + "F62", {"entities" : qUnion([Q0, Q1, Q2, Q3, Q4, Q5, Q6, Q7, Q8, Q9, Q10, Q11]), "operationType" : NewBodyOperationType.REMOVE, "depth" : 100.4 * mm, "offsetDistance" : 25 * mm});
        }
        {
            var Q0;
            Q0=makeQuery(id+"F13.boolean.opBoolean","INTERSECT",EDGE,{"derivedFrom":[makeQuery(id+"F1.opExtrude","SWEPT_FACE",FACE,{"disambiguationData":[OSD([sQuery(id+"F0.wireOp",EDGE,"E4")])]}),makeQuery(id+"F13.opExtrude","SWEPT_FACE",FACE,{"disambiguationData":[OSD([sQuery(id+"F11.wireOp",EDGE,"E35")])]})]});
            var Q1;
            Q1=makeQuery(id+"F46.opFillet","BLEND_EDGE",EDGE,{"blendedFrom":[makeQuery(id+"F1.opExtrude","CAP_EDGE",EDGE,{"disambiguationData":[OSD([sQuery(id+"F0.wireOp",EDGE,"E4")])],"isStart":true}),makeQuery(id+"F13.boolean.opBoolean","COPY",FACE,{"derivedFrom":makeQuery(id+"F13.opExtrude","SWEPT_FACE",FACE,{"disambiguationData":[OSD([sQuery(id+"F11.wireOp",EDGE,"E35")])]})})],"blendedInto":[makeQuery(id+"F13.boolean.opBoolean","COPY",FACE,{"derivedFrom":makeQuery(id+"F13.opExtrude","SWEPT_FACE",FACE,{"disambiguationData":[OSD([sQuery(id+"F11.wireOp",EDGE,"E35")])]})})]});
            var Q2;
            Q2=makeQuery(id+"F13.boolean.opBoolean","INTERSECT",EDGE,{"derivedFrom":[makeQuery(id+"F1.opExtrude","SWEPT_FACE",FACE,{"disambiguationData":[OSD([sQuery(id+"F0.wireOp",EDGE,"E14.filletArc")])]}),makeQuery(id+"F13.opExtrude","SWEPT_FACE",FACE,{"disambiguationData":[OSD([sQuery(id+"F11.wireOp",EDGE,"E35")])]})]});
            var Q3;
            Q3=makeQuery(id+"F6.boolean.opBoolean","INTERSECT",EDGE,{"derivedFrom":[makeQuery(id+"F1.opExtrude","SWEPT_FACE",FACE,{"disambiguationData":[OSD([sQuery(id+"F0.wireOp",EDGE,"E4")])]}),makeQuery(id+"F6.opExtrude","SWEPT_FACE",FACE,{"disambiguationData":[OSD([sQuery(id+"F4.wireOp",EDGE,"E30.MirrorC")])]})]});
            var Q4;
            Q4=makeQuery(id+"F6.boolean.opBoolean","INTERSECT",EDGE,{"derivedFrom":[makeQuery(id+"F1.opExtrude","SWEPT_FACE",FACE,{"disambiguationData":[OSD([sQuery(id+"F0.wireOp",EDGE,"E4")])]}),makeQuery(id+"F6.opExtrude","SWEPT_FACE",FACE,{"disambiguationData":[OSD([sQuery(id+"F4.wireOp",EDGE,"E28")])]})]});
            var Q5;
            Q5=makeQuery(id+"F13.boolean.opBoolean","INTERSECT",EDGE,{"derivedFrom":[makeQuery(id+"F1.opExtrude","SWEPT_FACE",FACE,{"disambiguationData":[OSD([sQuery(id+"F0.wireOp",EDGE,"E4")])]}),makeQuery(id+"F13.opExtrude","SWEPT_FACE",FACE,{"disambiguationData":[OSD([sQuery(id+"F11.wireOp",EDGE,"E40")])]})]});
            var Q6;
            Q6=makeQuery(id+"F46.opFillet","BLEND_EDGE",EDGE,{"blendedFrom":[makeQuery(id+"F1.opExtrude","CAP_EDGE",EDGE,{"disambiguationData":[OSD([sQuery(id+"F0.wireOp",EDGE,"E4")])],"isStart":false}),makeQuery(id+"F13.boolean.opBoolean","COPY",FACE,{"derivedFrom":makeQuery(id+"F13.opExtrude","SWEPT_FACE",FACE,{"disambiguationData":[OSD([sQuery(id+"F11.wireOp",EDGE,"E40")])]})})],"blendedInto":[makeQuery(id+"F13.boolean.opBoolean","COPY",FACE,{"derivedFrom":makeQuery(id+"F13.opExtrude","SWEPT_FACE",FACE,{"disambiguationData":[OSD([sQuery(id+"F11.wireOp",EDGE,"E40")])]})})]});
            fillet(context, id + "F63", {"entities" : qUnion([Q0, Q1, Q2, Q3, Q4, Q5, Q6]), "radius" : 1 * mm, "tangentPropagation" : true, "allowEdgeOverflow" : false});
        }
        {
            var Q0;
            Q0=makeQuery(id+"F62.boolean.opBoolean","INTERSECT",EDGE,{"disambiguationData":[OD(1.0)],"derivedFrom":[makeQuery(id+"F1.opExtrude","CAP_FACE",FACE,{"disambiguationData":[OSD([sQuery(id+"F0.wireOp",EDGE,"E4"),sQuery(id+"F0.wireOp",EDGE,"E5"),sQuery(id+"F0.wireOp",EDGE,"E8"),sQuery(id+"F0.wireOp",EDGE,"E9"),sQuery(id+"F0.wireOp",EDGE,"E10.MirrorCS"),sQuery(id+"F0.wireOp",EDGE,"E11.filletArc"),sQuery(id+"F0.wireOp",EDGE,"E12.filletArc"),sQuery(id+"F0.wireOp",EDGE,"E13"),sQuery(id+"F0.wireOp",EDGE,"E14.filletArc"),sQuery(id+"F0.wireOp",EDGE,"E15.filletArc")])],"isStart":true}),makeQuery(id+"F62.opExtrude","SWEPT_FACE",FACE,{"disambiguationData":[OSD([sQuery(id+"F61.wireOp",EDGE,"E186")])]})]});
            fillet(context, id + "F64", {"entities" : qUnion([Q0]), "radius" : 4 * mm, "tangentPropagation" : true, "allowEdgeOverflow" : false});
        }
        {
            var Q0;
            Q0=makeQuery(id+"F62.boolean.opBoolean","COPY",FACE,{"derivedFrom":makeQuery(id+"F62.opExtrude","SWEPT_FACE",FACE,{"disambiguationData":[OSD([sQuery(id+"F61.wireOp",EDGE,"E183")])]})});
            fillet(context, id + "F65", {"entities" : qUnion([Q0]), "radius" : 6 * mm, "tangentPropagation" : true, "allowEdgeOverflow" : false});
        }
    });
